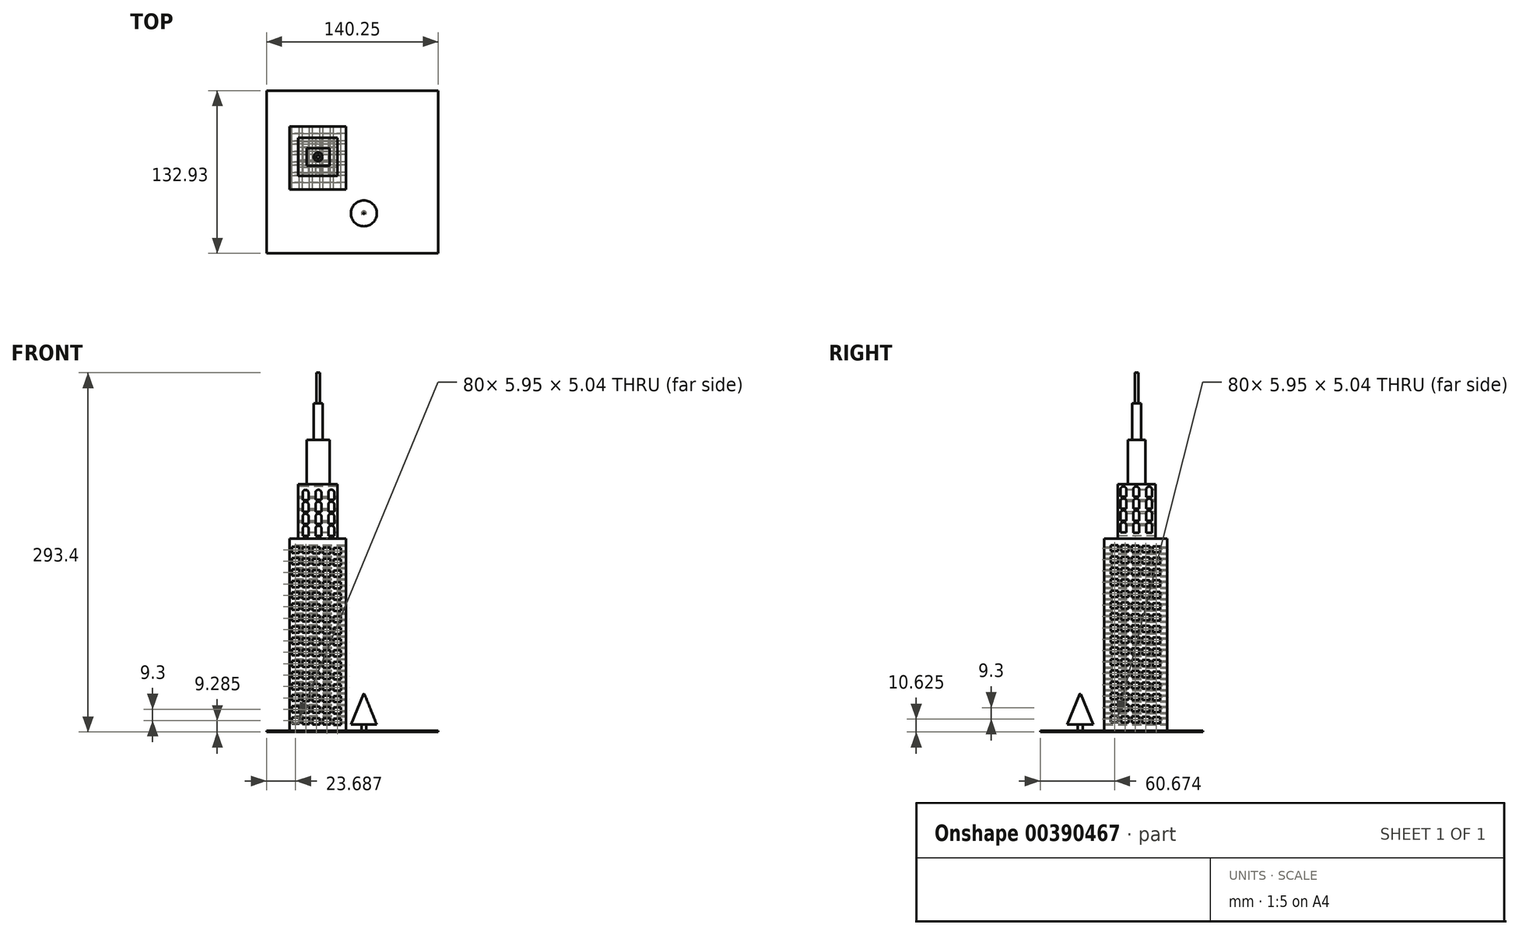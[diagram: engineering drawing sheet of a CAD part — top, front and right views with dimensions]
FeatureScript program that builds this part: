
annotation { "Feature Type Name" : "Feature", "Feature Type Description" : "" }
export const myFeature = defineFeature(function(context is Context, id is Id, definition is map)
    precondition{}
    {
        {
            var Q0;
            Q0=qCreatedBy(makeId("Top.planeOp"),FACE);
            var sketch = newSketch(context, id + "F0", { "sketchPlane" : qUnion([Q0])});
            skLineSegment(sketch, "E0.bottom", {"start": v(-71.35, 69.65) * mm, "end": v(68.9, 69.65) * mm});
            skLineSegment(sketch, "E0.top", {"start": v(-71.35, -63.28) * mm, "end": v(68.9, -63.28) * mm});
            skLineSegment(sketch, "E0.left", {"start": v(-71.35, 69.65) * mm, "end": v(-71.35, -63.28) * mm});
            skLineSegment(sketch, "E0.right", {"start": v(68.9, 69.65) * mm, "end": v(68.9, -63.28) * mm});
            skSolve(sketch);
        }
        {
            var Q0;
            Q0=makeQuery(id+"F0.imprint","IMPRINT",FACE,{"disambiguationData":[TD([[makeQuery(id+"F0.imprint","IMPRINT",EDGE,{"derivedFrom":sQuery(id+"F0.wireOp",EDGE,"E0.bottom")}),-1.0]])]});
            extrude(context, id + "F1", {"entities" : qUnion([Q0]), "depth" : 1 * mm});
        }
        {
            var Q0;
            Q0=makeQuery(id+"F1.opExtrude","CAP_FACE",FACE,{"disambiguationData":[OSD([sQuery(id+"F0.wireOp",EDGE,"E0.bottom"),sQuery(id+"F0.wireOp",EDGE,"E0.top"),sQuery(id+"F0.wireOp",EDGE,"E0.left"),sQuery(id+"F0.wireOp",EDGE,"E0.right")])],"isStart":false});
            var sketch = newSketch(context, id + "F2", { "sketchPlane" : qUnion([Q0])});
            skLineSegment(sketch, "E1.bottom", {"start": v(-52.6, 40.36) * mm, "end": v(-6.42, 40.36) * mm});
            skLineSegment(sketch, "E1.top", {"start": v(-52.6, -11.24) * mm, "end": v(-6.42, -11.24) * mm});
            skLineSegment(sketch, "E1.left", {"start": v(-52.6, 40.36) * mm, "end": v(-52.6, -11.24) * mm});
            skLineSegment(sketch, "E1.right", {"start": v(-6.42, 40.36) * mm, "end": v(-6.42, -11.24) * mm});
            skSolve(sketch);
        }
        {
            var Q0;
            Q0=makeQuery(id+"F2.imprint","IMPRINT",FACE,{"disambiguationData":[TD([[makeQuery(id+"F2.imprint","IMPRINT",EDGE,{"derivedFrom":sQuery(id+"F2.wireOp",EDGE,"E1.bottom")}),-1.0]])]});
            extrude(context, id + "F3", {"entities" : qUnion([Q0]), "operationType" : NewBodyOperationType.ADD, "depth" : 157 * mm});
        }
        {
            var Q0;
            Q0=makeQuery(id+"F3.opExtrude","CAP_FACE",FACE,{"disambiguationData":[OSD([sQuery(id+"F2.wireOp",EDGE,"E1.bottom"),sQuery(id+"F2.wireOp",EDGE,"E1.top"),sQuery(id+"F2.wireOp",EDGE,"E1.left"),sQuery(id+"F2.wireOp",EDGE,"E1.right")])],"isStart":false});
            var sketch = newSketch(context, id + "F4", { "sketchPlane" : qUnion([Q0])});
            skLineSegment(sketch, "E2.bottom", {"start": v(-45.38, 30.95) * mm, "end": v(-13.57, 30.95) * mm});
            skLineSegment(sketch, "E2.top", {"start": v(-45.38, 0) * mm, "end": v(-13.57, 0) * mm});
            skLineSegment(sketch, "E2.left", {"start": v(-45.38, 30.95) * mm, "end": v(-45.38, 0) * mm});
            skLineSegment(sketch, "E2.right", {"start": v(-13.57, 30.95) * mm, "end": v(-13.57, 0) * mm});
            skSolve(sketch);
        }
        {
            var Q0;
            Q0=makeQuery(id+"F4.imprint","IMPRINT",FACE,{"disambiguationData":[TD([[makeQuery(id+"F4.imprint","IMPRINT",EDGE,{"derivedFrom":sQuery(id+"F4.wireOp",EDGE,"E2.bottom")}),-1.0]])]});
            extrude(context, id + "F5", {"entities" : qUnion([Q0]), "operationType" : NewBodyOperationType.ADD, "depth" : 44.3 * mm});
        }
        {
            var Q0;
            Q0=makeQuery(id+"F5.opExtrude","CAP_FACE",FACE,{"disambiguationData":[OSD([sQuery(id+"F4.wireOp",EDGE,"E2.bottom"),sQuery(id+"F4.wireOp",EDGE,"E2.top"),sQuery(id+"F4.wireOp",EDGE,"E2.left"),sQuery(id+"F4.wireOp",EDGE,"E2.right")])],"isStart":false});
            var sketch = newSketch(context, id + "F6", { "sketchPlane" : qUnion([Q0])});
            skLineSegment(sketch, "E3.bottom", {"start": v(-38.58, 22.65) * mm, "end": v(-19.77, 22.65) * mm});
            skLineSegment(sketch, "E3.top", {"start": v(-38.58, 8.27) * mm, "end": v(-19.77, 8.27) * mm});
            skLineSegment(sketch, "E3.left", {"start": v(-38.58, 22.65) * mm, "end": v(-38.58, 8.27) * mm});
            skLineSegment(sketch, "E3.right", {"start": v(-19.77, 22.65) * mm, "end": v(-19.77, 8.27) * mm});
            skSolve(sketch);
        }
        {
            var Q0;
            Q0=makeQuery(id+"F6.imprint","IMPRINT",FACE,{"disambiguationData":[TD([[makeQuery(id+"F6.imprint","IMPRINT",EDGE,{"derivedFrom":sQuery(id+"F6.wireOp",EDGE,"E3.bottom")}),-1.0]])]});
            extrude(context, id + "F7", {"entities" : qUnion([Q0]), "operationType" : NewBodyOperationType.ADD, "depth" : 36.3 * mm});
        }
        {
            var Q0;
            Q0=makeQuery(id+"F7.opExtrude","CAP_FACE",FACE,{"disambiguationData":[OSD([sQuery(id+"F6.wireOp",EDGE,"E3.bottom"),sQuery(id+"F6.wireOp",EDGE,"E3.top"),sQuery(id+"F6.wireOp",EDGE,"E3.left"),sQuery(id+"F6.wireOp",EDGE,"E3.right")])],"isStart":false});
            var sketch = newSketch(context, id + "F8", { "sketchPlane" : qUnion([Q0])});
            skCircle(sketch, "E4", {"center": v(-29.18, 15.46) * mm, "radius": 3.56 * mm});
            skPoint(sketch, "E4.centerSnap0", {"position": v(-19.77, 15.46) * mm});
            skPoint(sketch, "E4.centerSnap1", {"position": v(-29.18, 22.65) * mm});
            skSolve(sketch);
        }
        {
            var Q0;
            Q0=makeQuery(id+"F8.imprint","IMPRINT",FACE,{"disambiguationData":[TD([[makeQuery(id+"F8.imprint","IMPRINT",EDGE,{"derivedFrom":sQuery(id+"F8.wireOp",EDGE,"E4")}),1.0]])]});
            extrude(context, id + "F9", {"entities" : qUnion([Q0]), "operationType" : NewBodyOperationType.ADD, "depth" : 29.8 * mm});
        }
        {
            var Q0;
            Q0=makeQuery(id+"F9.opExtrude","CAP_FACE",FACE,{"disambiguationData":[OSD([sQuery(id+"F8.wireOp",EDGE,"E4")])],"isStart":false});
            var sketch = newSketch(context, id + "F10", { "sketchPlane" : qUnion([Q0])});
            skCircle(sketch, "E5", {"center": v(-29.18, 15.46) * mm, "radius": 1.47 * mm});
            skSolve(sketch);
        }
        {
            var Q0;
            Q0=makeQuery(id+"F10.imprint","IMPRINT",FACE,{"disambiguationData":[TD([[makeQuery(id+"F10.imprint","IMPRINT",EDGE,{"derivedFrom":sQuery(id+"F10.wireOp",EDGE,"E5")}),1.0]])]});
            extrude(context, id + "F11", {"entities" : qUnion([Q0]), "operationType" : NewBodyOperationType.ADD, "depth" : 25 * mm});
        }
        {
            var Q0;
            Q0=makeQuery(id+"F3.opExtrude","SWEPT_FACE",FACE,{"disambiguationData":[OSD([sQuery(id+"F2.wireOp",EDGE,"E1.bottom")])]});
            var sketch = newSketch(context, id + "F12", { "sketchPlane" : qUnion([Q0])});
            skLineSegment(sketch, "E6.bottom", {"start": v(10.57, 10.87) * mm, "end": v(16.52, 10.87) * mm});
            skLineSegment(sketch, "E6.top", {"start": v(10.57, 5.83) * mm, "end": v(16.52, 5.83) * mm});
            skLineSegment(sketch, "E6.left", {"start": v(10.57, 10.87) * mm, "end": v(10.57, 5.83) * mm});
            skLineSegment(sketch, "E6.right", {"start": v(16.52, 10.87) * mm, "end": v(16.52, 5.83) * mm});
            skLineSegment(sketch, "E7.0.1.0", {"start": v(10.57, 20.17) * mm, "end": v(16.52, 20.17) * mm});
            skLineSegment(sketch, "E7.0.1.1", {"start": v(16.52, 20.17) * mm, "end": v(16.52, 15.13) * mm});
            skLineSegment(sketch, "E7.0.1.2", {"start": v(10.57, 15.13) * mm, "end": v(16.52, 15.13) * mm});
            skLineSegment(sketch, "E7.0.1.3", {"start": v(10.57, 20.17) * mm, "end": v(10.57, 15.13) * mm});
            skLineSegment(sketch, "E7.0.2.0", {"start": v(10.57, 29.47) * mm, "end": v(16.52, 29.47) * mm});
            skLineSegment(sketch, "E7.0.2.1", {"start": v(16.52, 29.47) * mm, "end": v(16.52, 24.43) * mm});
            skLineSegment(sketch, "E7.0.2.2", {"start": v(10.57, 24.43) * mm, "end": v(16.52, 24.43) * mm});
            skLineSegment(sketch, "E7.0.2.3", {"start": v(10.57, 29.47) * mm, "end": v(10.57, 24.43) * mm});
            skLineSegment(sketch, "E7.0.3.0", {"start": v(10.57, 38.77) * mm, "end": v(16.52, 38.77) * mm});
            skLineSegment(sketch, "E7.0.3.1", {"start": v(16.52, 38.77) * mm, "end": v(16.52, 33.73) * mm});
            skLineSegment(sketch, "E7.0.3.2", {"start": v(10.57, 33.73) * mm, "end": v(16.52, 33.73) * mm});
            skLineSegment(sketch, "E7.0.3.3", {"start": v(10.57, 38.77) * mm, "end": v(10.57, 33.73) * mm});
            skLineSegment(sketch, "E7.0.4.0", {"start": v(10.57, 48.07) * mm, "end": v(16.52, 48.07) * mm});
            skLineSegment(sketch, "E7.0.4.1", {"start": v(16.52, 48.07) * mm, "end": v(16.52, 43.03) * mm});
            skLineSegment(sketch, "E7.0.4.2", {"start": v(10.57, 43.03) * mm, "end": v(16.52, 43.03) * mm});
            skLineSegment(sketch, "E7.0.4.3", {"start": v(10.57, 48.07) * mm, "end": v(10.57, 43.03) * mm});
            skLineSegment(sketch, "E7.0.5.0", {"start": v(10.57, 57.37) * mm, "end": v(16.52, 57.37) * mm});
            skLineSegment(sketch, "E7.0.5.1", {"start": v(16.52, 57.37) * mm, "end": v(16.52, 52.33) * mm});
            skLineSegment(sketch, "E7.0.5.2", {"start": v(10.57, 52.33) * mm, "end": v(16.52, 52.33) * mm});
            skLineSegment(sketch, "E7.0.5.3", {"start": v(10.57, 57.37) * mm, "end": v(10.57, 52.33) * mm});
            skLineSegment(sketch, "E7.0.6.0", {"start": v(10.57, 66.67) * mm, "end": v(16.52, 66.67) * mm});
            skLineSegment(sketch, "E7.0.6.1", {"start": v(16.52, 66.67) * mm, "end": v(16.52, 61.63) * mm});
            skLineSegment(sketch, "E7.0.6.2", {"start": v(10.57, 61.63) * mm, "end": v(16.52, 61.63) * mm});
            skLineSegment(sketch, "E7.0.6.3", {"start": v(10.57, 66.67) * mm, "end": v(10.57, 61.63) * mm});
            skLineSegment(sketch, "E7.0.7.0", {"start": v(10.57, 75.97) * mm, "end": v(16.52, 75.97) * mm});
            skLineSegment(sketch, "E7.0.7.1", {"start": v(16.52, 75.97) * mm, "end": v(16.52, 70.93) * mm});
            skLineSegment(sketch, "E7.0.7.2", {"start": v(10.57, 70.93) * mm, "end": v(16.52, 70.93) * mm});
            skLineSegment(sketch, "E7.0.7.3", {"start": v(10.57, 75.97) * mm, "end": v(10.57, 70.93) * mm});
            skLineSegment(sketch, "E7.0.8.0", {"start": v(10.57, 85.27) * mm, "end": v(16.52, 85.27) * mm});
            skLineSegment(sketch, "E7.0.8.1", {"start": v(16.52, 85.27) * mm, "end": v(16.52, 80.23) * mm});
            skLineSegment(sketch, "E7.0.8.2", {"start": v(10.57, 80.23) * mm, "end": v(16.52, 80.23) * mm});
            skLineSegment(sketch, "E7.0.8.3", {"start": v(10.57, 85.27) * mm, "end": v(10.57, 80.23) * mm});
            skLineSegment(sketch, "E7.0.9.0", {"start": v(10.57, 94.57) * mm, "end": v(16.52, 94.57) * mm});
            skLineSegment(sketch, "E7.0.9.1", {"start": v(16.52, 94.57) * mm, "end": v(16.52, 89.53) * mm});
            skLineSegment(sketch, "E7.0.9.2", {"start": v(10.57, 89.53) * mm, "end": v(16.52, 89.53) * mm});
            skLineSegment(sketch, "E7.0.9.3", {"start": v(10.57, 94.57) * mm, "end": v(10.57, 89.53) * mm});
            skLineSegment(sketch, "E7.1.0.0", {"start": v(19.1, 11.1) * mm, "end": v(25.05, 11.1) * mm});
            skLineSegment(sketch, "E7.1.0.1", {"start": v(25.05, 11.1) * mm, "end": v(25.05, 6.06) * mm});
            skLineSegment(sketch, "E7.1.0.2", {"start": v(19.1, 6.06) * mm, "end": v(25.05, 6.06) * mm});
            skLineSegment(sketch, "E7.1.0.3", {"start": v(19.1, 11.1) * mm, "end": v(19.1, 6.06) * mm});
            skLineSegment(sketch, "E7.1.1.0", {"start": v(19.1, 20.4) * mm, "end": v(25.05, 20.4) * mm});
            skLineSegment(sketch, "E7.1.1.1", {"start": v(25.05, 20.4) * mm, "end": v(25.05, 15.36) * mm});
            skLineSegment(sketch, "E7.1.1.2", {"start": v(19.1, 15.36) * mm, "end": v(25.05, 15.36) * mm});
            skLineSegment(sketch, "E7.1.1.3", {"start": v(19.1, 20.4) * mm, "end": v(19.1, 15.36) * mm});
            skLineSegment(sketch, "E7.1.2.0", {"start": v(19.1, 29.7) * mm, "end": v(25.05, 29.7) * mm});
            skLineSegment(sketch, "E7.1.2.1", {"start": v(25.05, 29.7) * mm, "end": v(25.05, 24.66) * mm});
            skLineSegment(sketch, "E7.1.2.2", {"start": v(19.1, 24.66) * mm, "end": v(25.05, 24.66) * mm});
            skLineSegment(sketch, "E7.1.2.3", {"start": v(19.1, 29.7) * mm, "end": v(19.1, 24.66) * mm});
            skLineSegment(sketch, "E7.1.3.0", {"start": v(19.1, 39) * mm, "end": v(25.05, 39) * mm});
            skLineSegment(sketch, "E7.1.3.1", {"start": v(25.05, 39) * mm, "end": v(25.05, 33.96) * mm});
            skLineSegment(sketch, "E7.1.3.2", {"start": v(19.1, 33.96) * mm, "end": v(25.05, 33.96) * mm});
            skLineSegment(sketch, "E7.1.3.3", {"start": v(19.1, 39) * mm, "end": v(19.1, 33.96) * mm});
            skLineSegment(sketch, "E7.1.4.0", {"start": v(19.1, 48.3) * mm, "end": v(25.05, 48.3) * mm});
            skLineSegment(sketch, "E7.1.4.1", {"start": v(25.05, 48.3) * mm, "end": v(25.05, 43.26) * mm});
            skLineSegment(sketch, "E7.1.4.2", {"start": v(19.1, 43.26) * mm, "end": v(25.05, 43.26) * mm});
            skLineSegment(sketch, "E7.1.4.3", {"start": v(19.1, 48.3) * mm, "end": v(19.1, 43.26) * mm});
            skLineSegment(sketch, "E7.1.5.0", {"start": v(19.1, 57.6) * mm, "end": v(25.05, 57.6) * mm});
            skLineSegment(sketch, "E7.1.5.1", {"start": v(25.05, 57.6) * mm, "end": v(25.05, 52.56) * mm});
            skLineSegment(sketch, "E7.1.5.2", {"start": v(19.1, 52.56) * mm, "end": v(25.05, 52.56) * mm});
            skLineSegment(sketch, "E7.1.5.3", {"start": v(19.1, 57.6) * mm, "end": v(19.1, 52.56) * mm});
            skLineSegment(sketch, "E7.1.6.0", {"start": v(19.1, 66.9) * mm, "end": v(25.05, 66.9) * mm});
            skLineSegment(sketch, "E7.1.6.1", {"start": v(25.05, 66.9) * mm, "end": v(25.05, 61.86) * mm});
            skLineSegment(sketch, "E7.1.6.2", {"start": v(19.1, 61.86) * mm, "end": v(25.05, 61.86) * mm});
            skLineSegment(sketch, "E7.1.6.3", {"start": v(19.1, 66.9) * mm, "end": v(19.1, 61.86) * mm});
            skLineSegment(sketch, "E7.1.7.0", {"start": v(19.1, 76.2) * mm, "end": v(25.05, 76.2) * mm});
            skLineSegment(sketch, "E7.1.7.1", {"start": v(25.05, 76.2) * mm, "end": v(25.05, 71.16) * mm});
            skLineSegment(sketch, "E7.1.7.2", {"start": v(19.1, 71.16) * mm, "end": v(25.05, 71.16) * mm});
            skLineSegment(sketch, "E7.1.7.3", {"start": v(19.1, 76.2) * mm, "end": v(19.1, 71.16) * mm});
            skLineSegment(sketch, "E7.1.8.0", {"start": v(19.1, 85.5) * mm, "end": v(25.05, 85.5) * mm});
            skLineSegment(sketch, "E7.1.8.1", {"start": v(25.05, 85.5) * mm, "end": v(25.05, 80.46) * mm});
            skLineSegment(sketch, "E7.1.8.2", {"start": v(19.1, 80.46) * mm, "end": v(25.05, 80.46) * mm});
            skLineSegment(sketch, "E7.1.8.3", {"start": v(19.1, 85.5) * mm, "end": v(19.1, 80.46) * mm});
            skLineSegment(sketch, "E7.1.9.0", {"start": v(19.1, 94.8) * mm, "end": v(25.05, 94.8) * mm});
            skLineSegment(sketch, "E7.1.9.1", {"start": v(25.05, 94.8) * mm, "end": v(25.05, 89.76) * mm});
            skLineSegment(sketch, "E7.1.9.2", {"start": v(19.1, 89.76) * mm, "end": v(25.05, 89.76) * mm});
            skLineSegment(sketch, "E7.1.9.3", {"start": v(19.1, 94.8) * mm, "end": v(19.1, 89.76) * mm});
            skLineSegment(sketch, "E7.2.0.0", {"start": v(27.63, 11.33) * mm, "end": v(33.58, 11.33) * mm});
            skLineSegment(sketch, "E7.2.0.1", {"start": v(33.58, 11.33) * mm, "end": v(33.58, 6.3) * mm});
            skLineSegment(sketch, "E7.2.0.2", {"start": v(27.63, 6.3) * mm, "end": v(33.58, 6.3) * mm});
            skLineSegment(sketch, "E7.2.0.3", {"start": v(27.63, 11.33) * mm, "end": v(27.63, 6.3) * mm});
            skLineSegment(sketch, "E7.2.1.0", {"start": v(27.63, 20.63) * mm, "end": v(33.58, 20.63) * mm});
            skLineSegment(sketch, "E7.2.1.1", {"start": v(33.58, 20.63) * mm, "end": v(33.58, 15.6) * mm});
            skLineSegment(sketch, "E7.2.1.2", {"start": v(27.63, 15.6) * mm, "end": v(33.58, 15.6) * mm});
            skLineSegment(sketch, "E7.2.1.3", {"start": v(27.63, 20.63) * mm, "end": v(27.63, 15.6) * mm});
            skLineSegment(sketch, "E7.2.2.0", {"start": v(27.63, 29.93) * mm, "end": v(33.58, 29.93) * mm});
            skLineSegment(sketch, "E7.2.2.1", {"start": v(33.58, 29.93) * mm, "end": v(33.58, 24.9) * mm});
            skLineSegment(sketch, "E7.2.2.2", {"start": v(27.63, 24.9) * mm, "end": v(33.58, 24.9) * mm});
            skLineSegment(sketch, "E7.2.2.3", {"start": v(27.63, 29.93) * mm, "end": v(27.63, 24.9) * mm});
            skLineSegment(sketch, "E7.2.3.0", {"start": v(27.63, 39.23) * mm, "end": v(33.58, 39.23) * mm});
            skLineSegment(sketch, "E7.2.3.1", {"start": v(33.58, 39.23) * mm, "end": v(33.58, 34.2) * mm});
            skLineSegment(sketch, "E7.2.3.2", {"start": v(27.63, 34.2) * mm, "end": v(33.58, 34.2) * mm});
            skLineSegment(sketch, "E7.2.3.3", {"start": v(27.63, 39.23) * mm, "end": v(27.63, 34.2) * mm});
            skLineSegment(sketch, "E7.2.4.0", {"start": v(27.63, 48.53) * mm, "end": v(33.58, 48.53) * mm});
            skLineSegment(sketch, "E7.2.4.1", {"start": v(33.58, 48.53) * mm, "end": v(33.58, 43.5) * mm});
            skLineSegment(sketch, "E7.2.4.2", {"start": v(27.63, 43.5) * mm, "end": v(33.58, 43.5) * mm});
            skLineSegment(sketch, "E7.2.4.3", {"start": v(27.63, 48.53) * mm, "end": v(27.63, 43.5) * mm});
            skLineSegment(sketch, "E7.2.5.0", {"start": v(27.63, 57.83) * mm, "end": v(33.58, 57.83) * mm});
            skLineSegment(sketch, "E7.2.5.1", {"start": v(33.58, 57.83) * mm, "end": v(33.58, 52.8) * mm});
            skLineSegment(sketch, "E7.2.5.2", {"start": v(27.63, 52.8) * mm, "end": v(33.58, 52.8) * mm});
            skLineSegment(sketch, "E7.2.5.3", {"start": v(27.63, 57.83) * mm, "end": v(27.63, 52.8) * mm});
            skLineSegment(sketch, "E7.2.6.0", {"start": v(27.63, 67.13) * mm, "end": v(33.58, 67.13) * mm});
            skLineSegment(sketch, "E7.2.6.1", {"start": v(33.58, 67.13) * mm, "end": v(33.58, 62.1) * mm});
            skLineSegment(sketch, "E7.2.6.2", {"start": v(27.63, 62.1) * mm, "end": v(33.58, 62.1) * mm});
            skLineSegment(sketch, "E7.2.6.3", {"start": v(27.63, 67.13) * mm, "end": v(27.63, 62.1) * mm});
            skLineSegment(sketch, "E7.2.7.0", {"start": v(27.63, 76.43) * mm, "end": v(33.58, 76.43) * mm});
            skLineSegment(sketch, "E7.2.7.1", {"start": v(33.58, 76.43) * mm, "end": v(33.58, 71.4) * mm});
            skLineSegment(sketch, "E7.2.7.2", {"start": v(27.63, 71.4) * mm, "end": v(33.58, 71.4) * mm});
            skLineSegment(sketch, "E7.2.7.3", {"start": v(27.63, 76.43) * mm, "end": v(27.63, 71.4) * mm});
            skLineSegment(sketch, "E7.2.8.0", {"start": v(27.63, 85.73) * mm, "end": v(33.58, 85.73) * mm});
            skLineSegment(sketch, "E7.2.8.1", {"start": v(33.58, 85.73) * mm, "end": v(33.58, 80.7) * mm});
            skLineSegment(sketch, "E7.2.8.2", {"start": v(27.63, 80.7) * mm, "end": v(33.58, 80.7) * mm});
            skLineSegment(sketch, "E7.2.8.3", {"start": v(27.63, 85.73) * mm, "end": v(27.63, 80.7) * mm});
            skLineSegment(sketch, "E7.2.9.0", {"start": v(27.63, 95.03) * mm, "end": v(33.58, 95.03) * mm});
            skLineSegment(sketch, "E7.2.9.1", {"start": v(33.58, 95.03) * mm, "end": v(33.58, 90) * mm});
            skLineSegment(sketch, "E7.2.9.2", {"start": v(27.63, 90) * mm, "end": v(33.58, 90) * mm});
            skLineSegment(sketch, "E7.2.9.3", {"start": v(27.63, 95.03) * mm, "end": v(27.63, 90) * mm});
            skLineSegment(sketch, "E7.3.0.0", {"start": v(36.16, 11.57) * mm, "end": v(42.11, 11.57) * mm});
            skLineSegment(sketch, "E7.3.0.1", {"start": v(42.11, 11.57) * mm, "end": v(42.11, 6.53) * mm});
            skLineSegment(sketch, "E7.3.0.2", {"start": v(36.16, 6.53) * mm, "end": v(42.11, 6.53) * mm});
            skLineSegment(sketch, "E7.3.0.3", {"start": v(36.16, 11.57) * mm, "end": v(36.16, 6.53) * mm});
            skLineSegment(sketch, "E7.3.1.0", {"start": v(36.16, 20.87) * mm, "end": v(42.11, 20.87) * mm});
            skLineSegment(sketch, "E7.3.1.1", {"start": v(42.11, 20.87) * mm, "end": v(42.11, 15.83) * mm});
            skLineSegment(sketch, "E7.3.1.2", {"start": v(36.16, 15.83) * mm, "end": v(42.11, 15.83) * mm});
            skLineSegment(sketch, "E7.3.1.3", {"start": v(36.16, 20.87) * mm, "end": v(36.16, 15.83) * mm});
            skLineSegment(sketch, "E7.3.2.0", {"start": v(36.16, 30.17) * mm, "end": v(42.11, 30.17) * mm});
            skLineSegment(sketch, "E7.3.2.1", {"start": v(42.11, 30.17) * mm, "end": v(42.11, 25.13) * mm});
            skLineSegment(sketch, "E7.3.2.2", {"start": v(36.16, 25.13) * mm, "end": v(42.11, 25.13) * mm});
            skLineSegment(sketch, "E7.3.2.3", {"start": v(36.16, 30.17) * mm, "end": v(36.16, 25.13) * mm});
            skLineSegment(sketch, "E7.3.3.0", {"start": v(36.16, 39.47) * mm, "end": v(42.11, 39.47) * mm});
            skLineSegment(sketch, "E7.3.3.1", {"start": v(42.11, 39.47) * mm, "end": v(42.11, 34.43) * mm});
            skLineSegment(sketch, "E7.3.3.2", {"start": v(36.16, 34.43) * mm, "end": v(42.11, 34.43) * mm});
            skLineSegment(sketch, "E7.3.3.3", {"start": v(36.16, 39.47) * mm, "end": v(36.16, 34.43) * mm});
            skLineSegment(sketch, "E7.3.4.0", {"start": v(36.16, 48.77) * mm, "end": v(42.11, 48.77) * mm});
            skLineSegment(sketch, "E7.3.4.1", {"start": v(42.11, 48.77) * mm, "end": v(42.11, 43.73) * mm});
            skLineSegment(sketch, "E7.3.4.2", {"start": v(36.16, 43.73) * mm, "end": v(42.11, 43.73) * mm});
            skLineSegment(sketch, "E7.3.4.3", {"start": v(36.16, 48.77) * mm, "end": v(36.16, 43.73) * mm});
            skLineSegment(sketch, "E7.3.5.0", {"start": v(36.16, 58.07) * mm, "end": v(42.11, 58.07) * mm});
            skLineSegment(sketch, "E7.3.5.1", {"start": v(42.11, 58.07) * mm, "end": v(42.11, 53.03) * mm});
            skLineSegment(sketch, "E7.3.5.2", {"start": v(36.16, 53.03) * mm, "end": v(42.11, 53.03) * mm});
            skLineSegment(sketch, "E7.3.5.3", {"start": v(36.16, 58.07) * mm, "end": v(36.16, 53.03) * mm});
            skLineSegment(sketch, "E7.3.6.0", {"start": v(36.16, 67.37) * mm, "end": v(42.11, 67.37) * mm});
            skLineSegment(sketch, "E7.3.6.1", {"start": v(42.11, 67.37) * mm, "end": v(42.11, 62.33) * mm});
            skLineSegment(sketch, "E7.3.6.2", {"start": v(36.16, 62.33) * mm, "end": v(42.11, 62.33) * mm});
            skLineSegment(sketch, "E7.3.6.3", {"start": v(36.16, 67.37) * mm, "end": v(36.16, 62.33) * mm});
            skLineSegment(sketch, "E7.3.7.0", {"start": v(36.16, 76.67) * mm, "end": v(42.11, 76.67) * mm});
            skLineSegment(sketch, "E7.3.7.1", {"start": v(42.11, 76.67) * mm, "end": v(42.11, 71.63) * mm});
            skLineSegment(sketch, "E7.3.7.2", {"start": v(36.16, 71.63) * mm, "end": v(42.11, 71.63) * mm});
            skLineSegment(sketch, "E7.3.7.3", {"start": v(36.16, 76.67) * mm, "end": v(36.16, 71.63) * mm});
            skLineSegment(sketch, "E7.3.8.0", {"start": v(36.16, 85.97) * mm, "end": v(42.11, 85.97) * mm});
            skLineSegment(sketch, "E7.3.8.1", {"start": v(42.11, 85.97) * mm, "end": v(42.11, 80.93) * mm});
            skLineSegment(sketch, "E7.3.8.2", {"start": v(36.16, 80.93) * mm, "end": v(42.11, 80.93) * mm});
            skLineSegment(sketch, "E7.3.8.3", {"start": v(36.16, 85.97) * mm, "end": v(36.16, 80.93) * mm});
            skLineSegment(sketch, "E7.3.9.0", {"start": v(36.16, 95.27) * mm, "end": v(42.11, 95.27) * mm});
            skLineSegment(sketch, "E7.3.9.1", {"start": v(42.11, 95.27) * mm, "end": v(42.11, 90.23) * mm});
            skLineSegment(sketch, "E7.3.9.2", {"start": v(36.16, 90.23) * mm, "end": v(42.11, 90.23) * mm});
            skLineSegment(sketch, "E7.3.9.3", {"start": v(36.16, 95.27) * mm, "end": v(36.16, 90.23) * mm});
            skLineSegment(sketch, "E7.4.0.0", {"start": v(44.69, 11.8) * mm, "end": v(50.64, 11.8) * mm});
            skLineSegment(sketch, "E7.4.0.1", {"start": v(50.64, 11.8) * mm, "end": v(50.64, 6.77) * mm});
            skLineSegment(sketch, "E7.4.0.2", {"start": v(44.69, 6.77) * mm, "end": v(50.64, 6.77) * mm});
            skLineSegment(sketch, "E7.4.0.3", {"start": v(44.69, 11.8) * mm, "end": v(44.69, 6.77) * mm});
            skLineSegment(sketch, "E7.4.1.0", {"start": v(44.69, 21.1) * mm, "end": v(50.64, 21.1) * mm});
            skLineSegment(sketch, "E7.4.1.1", {"start": v(50.64, 21.1) * mm, "end": v(50.64, 16.07) * mm});
            skLineSegment(sketch, "E7.4.1.2", {"start": v(44.69, 16.07) * mm, "end": v(50.64, 16.07) * mm});
            skLineSegment(sketch, "E7.4.1.3", {"start": v(44.69, 21.1) * mm, "end": v(44.69, 16.07) * mm});
            skLineSegment(sketch, "E7.4.2.0", {"start": v(44.69, 30.4) * mm, "end": v(50.64, 30.4) * mm});
            skLineSegment(sketch, "E7.4.2.1", {"start": v(50.64, 30.4) * mm, "end": v(50.64, 25.37) * mm});
            skLineSegment(sketch, "E7.4.2.2", {"start": v(44.69, 25.37) * mm, "end": v(50.64, 25.37) * mm});
            skLineSegment(sketch, "E7.4.2.3", {"start": v(44.69, 30.4) * mm, "end": v(44.69, 25.37) * mm});
            skLineSegment(sketch, "E7.4.3.0", {"start": v(44.69, 39.7) * mm, "end": v(50.64, 39.7) * mm});
            skLineSegment(sketch, "E7.4.3.1", {"start": v(50.64, 39.7) * mm, "end": v(50.64, 34.67) * mm});
            skLineSegment(sketch, "E7.4.3.2", {"start": v(44.69, 34.67) * mm, "end": v(50.64, 34.67) * mm});
            skLineSegment(sketch, "E7.4.3.3", {"start": v(44.69, 39.7) * mm, "end": v(44.69, 34.67) * mm});
            skLineSegment(sketch, "E7.4.4.0", {"start": v(44.69, 49) * mm, "end": v(50.64, 49) * mm});
            skLineSegment(sketch, "E7.4.4.1", {"start": v(50.64, 49) * mm, "end": v(50.64, 43.97) * mm});
            skLineSegment(sketch, "E7.4.4.2", {"start": v(44.69, 43.97) * mm, "end": v(50.64, 43.97) * mm});
            skLineSegment(sketch, "E7.4.4.3", {"start": v(44.69, 49) * mm, "end": v(44.69, 43.97) * mm});
            skLineSegment(sketch, "E7.4.5.0", {"start": v(44.69, 58.3) * mm, "end": v(50.64, 58.3) * mm});
            skLineSegment(sketch, "E7.4.5.1", {"start": v(50.64, 58.3) * mm, "end": v(50.64, 53.27) * mm});
            skLineSegment(sketch, "E7.4.5.2", {"start": v(44.69, 53.27) * mm, "end": v(50.64, 53.27) * mm});
            skLineSegment(sketch, "E7.4.5.3", {"start": v(44.69, 58.3) * mm, "end": v(44.69, 53.27) * mm});
            skLineSegment(sketch, "E7.4.6.0", {"start": v(44.69, 67.6) * mm, "end": v(50.64, 67.6) * mm});
            skLineSegment(sketch, "E7.4.6.1", {"start": v(50.64, 67.6) * mm, "end": v(50.64, 62.57) * mm});
            skLineSegment(sketch, "E7.4.6.2", {"start": v(44.69, 62.57) * mm, "end": v(50.64, 62.57) * mm});
            skLineSegment(sketch, "E7.4.6.3", {"start": v(44.69, 67.6) * mm, "end": v(44.69, 62.57) * mm});
            skLineSegment(sketch, "E7.4.7.0", {"start": v(44.69, 76.9) * mm, "end": v(50.64, 76.9) * mm});
            skLineSegment(sketch, "E7.4.7.1", {"start": v(50.64, 76.9) * mm, "end": v(50.64, 71.87) * mm});
            skLineSegment(sketch, "E7.4.7.2", {"start": v(44.69, 71.87) * mm, "end": v(50.64, 71.87) * mm});
            skLineSegment(sketch, "E7.4.7.3", {"start": v(44.69, 76.9) * mm, "end": v(44.69, 71.87) * mm});
            skLineSegment(sketch, "E7.4.8.0", {"start": v(44.69, 86.2) * mm, "end": v(50.64, 86.2) * mm});
            skLineSegment(sketch, "E7.4.8.1", {"start": v(50.64, 86.2) * mm, "end": v(50.64, 81.17) * mm});
            skLineSegment(sketch, "E7.4.8.2", {"start": v(44.69, 81.17) * mm, "end": v(50.64, 81.17) * mm});
            skLineSegment(sketch, "E7.4.8.3", {"start": v(44.69, 86.2) * mm, "end": v(44.69, 81.17) * mm});
            skLineSegment(sketch, "E7.4.9.0", {"start": v(44.69, 95.5) * mm, "end": v(50.64, 95.5) * mm});
            skLineSegment(sketch, "E7.4.9.1", {"start": v(50.64, 95.5) * mm, "end": v(50.64, 90.47) * mm});
            skLineSegment(sketch, "E7.4.9.2", {"start": v(44.69, 90.47) * mm, "end": v(50.64, 90.47) * mm});
            skLineSegment(sketch, "E7.4.9.3", {"start": v(44.69, 95.5) * mm, "end": v(44.69, 90.47) * mm});
            skLineSegment(sketch, "E7.direction1", {"start": v(10.57, 10.87) * mm, "end": v(19.1, 11.1) * mm, "construction": true});
            skLineSegment(sketch, "E7.direction2", {"start": v(10.57, 10.87) * mm, "end": v(10.57, 20.17) * mm, "construction": true});
            skLineSegment(sketch, "E8.0.0.10", {"start": v(10.57, 103.87) * mm, "end": v(16.52, 103.87) * mm});
            skLineSegment(sketch, "E8.3.0.10", {"start": v(16.52, 103.87) * mm, "end": v(16.52, 98.83) * mm});
            skLineSegment(sketch, "E8.6.0.10", {"start": v(10.57, 98.83) * mm, "end": v(16.52, 98.83) * mm});
            skLineSegment(sketch, "E8.9.0.10", {"start": v(10.57, 103.87) * mm, "end": v(10.57, 98.83) * mm});
            skLineSegment(sketch, "E8.0.0.11", {"start": v(10.57, 113.17) * mm, "end": v(16.52, 113.17) * mm});
            skLineSegment(sketch, "E8.3.0.11", {"start": v(16.52, 113.17) * mm, "end": v(16.52, 108.13) * mm});
            skLineSegment(sketch, "E8.6.0.11", {"start": v(10.57, 108.13) * mm, "end": v(16.52, 108.13) * mm});
            skLineSegment(sketch, "E8.9.0.11", {"start": v(10.57, 113.17) * mm, "end": v(10.57, 108.13) * mm});
            skLineSegment(sketch, "E8.0.0.12", {"start": v(10.57, 122.47) * mm, "end": v(16.52, 122.47) * mm});
            skLineSegment(sketch, "E8.3.0.12", {"start": v(16.52, 122.47) * mm, "end": v(16.52, 117.43) * mm});
            skLineSegment(sketch, "E8.6.0.12", {"start": v(10.57, 117.43) * mm, "end": v(16.52, 117.43) * mm});
            skLineSegment(sketch, "E8.9.0.12", {"start": v(10.57, 122.47) * mm, "end": v(10.57, 117.43) * mm});
            skLineSegment(sketch, "E8.0.0.13", {"start": v(10.57, 131.77) * mm, "end": v(16.52, 131.77) * mm});
            skLineSegment(sketch, "E8.3.0.13", {"start": v(16.52, 131.77) * mm, "end": v(16.52, 126.73) * mm});
            skLineSegment(sketch, "E8.6.0.13", {"start": v(10.57, 126.73) * mm, "end": v(16.52, 126.73) * mm});
            skLineSegment(sketch, "E8.9.0.13", {"start": v(10.57, 131.77) * mm, "end": v(10.57, 126.73) * mm});
            skLineSegment(sketch, "E8.0.0.14", {"start": v(10.57, 141.07) * mm, "end": v(16.52, 141.07) * mm});
            skLineSegment(sketch, "E8.3.0.14", {"start": v(16.52, 141.07) * mm, "end": v(16.52, 136.03) * mm});
            skLineSegment(sketch, "E8.6.0.14", {"start": v(10.57, 136.03) * mm, "end": v(16.52, 136.03) * mm});
            skLineSegment(sketch, "E8.9.0.14", {"start": v(10.57, 141.07) * mm, "end": v(10.57, 136.03) * mm});
            skLineSegment(sketch, "E8.0.1.10", {"start": v(19.1, 104.1) * mm, "end": v(25.05, 104.1) * mm});
            skLineSegment(sketch, "E8.3.1.10", {"start": v(25.05, 104.1) * mm, "end": v(25.05, 99.06) * mm});
            skLineSegment(sketch, "E8.6.1.10", {"start": v(19.1, 99.06) * mm, "end": v(25.05, 99.06) * mm});
            skLineSegment(sketch, "E8.9.1.10", {"start": v(19.1, 104.1) * mm, "end": v(19.1, 99.06) * mm});
            skLineSegment(sketch, "E8.0.1.11", {"start": v(19.1, 113.4) * mm, "end": v(25.05, 113.4) * mm});
            skLineSegment(sketch, "E8.3.1.11", {"start": v(25.05, 113.4) * mm, "end": v(25.05, 108.36) * mm});
            skLineSegment(sketch, "E8.6.1.11", {"start": v(19.1, 108.36) * mm, "end": v(25.05, 108.36) * mm});
            skLineSegment(sketch, "E8.9.1.11", {"start": v(19.1, 113.4) * mm, "end": v(19.1, 108.36) * mm});
            skLineSegment(sketch, "E8.0.1.12", {"start": v(19.1, 122.7) * mm, "end": v(25.05, 122.7) * mm});
            skLineSegment(sketch, "E8.3.1.12", {"start": v(25.05, 122.7) * mm, "end": v(25.05, 117.66) * mm});
            skLineSegment(sketch, "E8.6.1.12", {"start": v(19.1, 117.66) * mm, "end": v(25.05, 117.66) * mm});
            skLineSegment(sketch, "E8.9.1.12", {"start": v(19.1, 122.7) * mm, "end": v(19.1, 117.66) * mm});
            skLineSegment(sketch, "E8.0.1.13", {"start": v(19.1, 132) * mm, "end": v(25.05, 132) * mm});
            skLineSegment(sketch, "E8.3.1.13", {"start": v(25.05, 132) * mm, "end": v(25.05, 126.96) * mm});
            skLineSegment(sketch, "E8.6.1.13", {"start": v(19.1, 126.96) * mm, "end": v(25.05, 126.96) * mm});
            skLineSegment(sketch, "E8.9.1.13", {"start": v(19.1, 132) * mm, "end": v(19.1, 126.96) * mm});
            skLineSegment(sketch, "E8.0.1.14", {"start": v(19.1, 141.3) * mm, "end": v(25.05, 141.3) * mm});
            skLineSegment(sketch, "E8.3.1.14", {"start": v(25.05, 141.3) * mm, "end": v(25.05, 136.26) * mm});
            skLineSegment(sketch, "E8.6.1.14", {"start": v(19.1, 136.26) * mm, "end": v(25.05, 136.26) * mm});
            skLineSegment(sketch, "E8.9.1.14", {"start": v(19.1, 141.3) * mm, "end": v(19.1, 136.26) * mm});
            skLineSegment(sketch, "E8.0.2.10", {"start": v(27.63, 104.33) * mm, "end": v(33.58, 104.33) * mm});
            skLineSegment(sketch, "E8.3.2.10", {"start": v(33.58, 104.33) * mm, "end": v(33.58, 99.3) * mm});
            skLineSegment(sketch, "E8.6.2.10", {"start": v(27.63, 99.3) * mm, "end": v(33.58, 99.3) * mm});
            skLineSegment(sketch, "E8.9.2.10", {"start": v(27.63, 104.33) * mm, "end": v(27.63, 99.3) * mm});
            skLineSegment(sketch, "E8.0.2.11", {"start": v(27.63, 113.63) * mm, "end": v(33.58, 113.63) * mm});
            skLineSegment(sketch, "E8.3.2.11", {"start": v(33.58, 113.63) * mm, "end": v(33.58, 108.6) * mm});
            skLineSegment(sketch, "E8.6.2.11", {"start": v(27.63, 108.6) * mm, "end": v(33.58, 108.6) * mm});
            skLineSegment(sketch, "E8.9.2.11", {"start": v(27.63, 113.63) * mm, "end": v(27.63, 108.6) * mm});
            skLineSegment(sketch, "E8.0.2.12", {"start": v(27.63, 122.93) * mm, "end": v(33.58, 122.93) * mm});
            skLineSegment(sketch, "E8.3.2.12", {"start": v(33.58, 122.93) * mm, "end": v(33.58, 117.9) * mm});
            skLineSegment(sketch, "E8.6.2.12", {"start": v(27.63, 117.9) * mm, "end": v(33.58, 117.9) * mm});
            skLineSegment(sketch, "E8.9.2.12", {"start": v(27.63, 122.93) * mm, "end": v(27.63, 117.9) * mm});
            skLineSegment(sketch, "E8.0.2.13", {"start": v(27.63, 132.23) * mm, "end": v(33.58, 132.23) * mm});
            skLineSegment(sketch, "E8.3.2.13", {"start": v(33.58, 132.23) * mm, "end": v(33.58, 127.2) * mm});
            skLineSegment(sketch, "E8.6.2.13", {"start": v(27.63, 127.2) * mm, "end": v(33.58, 127.2) * mm});
            skLineSegment(sketch, "E8.9.2.13", {"start": v(27.63, 132.23) * mm, "end": v(27.63, 127.2) * mm});
            skLineSegment(sketch, "E8.0.2.14", {"start": v(27.63, 141.53) * mm, "end": v(33.58, 141.53) * mm});
            skLineSegment(sketch, "E8.3.2.14", {"start": v(33.58, 141.53) * mm, "end": v(33.58, 136.5) * mm});
            skLineSegment(sketch, "E8.6.2.14", {"start": v(27.63, 136.5) * mm, "end": v(33.58, 136.5) * mm});
            skLineSegment(sketch, "E8.9.2.14", {"start": v(27.63, 141.53) * mm, "end": v(27.63, 136.5) * mm});
            skLineSegment(sketch, "E8.0.3.10", {"start": v(36.16, 104.57) * mm, "end": v(42.11, 104.57) * mm});
            skLineSegment(sketch, "E8.3.3.10", {"start": v(42.11, 104.57) * mm, "end": v(42.11, 99.53) * mm});
            skLineSegment(sketch, "E8.6.3.10", {"start": v(36.16, 99.53) * mm, "end": v(42.11, 99.53) * mm});
            skLineSegment(sketch, "E8.9.3.10", {"start": v(36.16, 104.57) * mm, "end": v(36.16, 99.53) * mm});
            skLineSegment(sketch, "E8.0.3.11", {"start": v(36.16, 113.87) * mm, "end": v(42.11, 113.87) * mm});
            skLineSegment(sketch, "E8.3.3.11", {"start": v(42.11, 113.87) * mm, "end": v(42.11, 108.83) * mm});
            skLineSegment(sketch, "E8.6.3.11", {"start": v(36.16, 108.83) * mm, "end": v(42.11, 108.83) * mm});
            skLineSegment(sketch, "E8.9.3.11", {"start": v(36.16, 113.87) * mm, "end": v(36.16, 108.83) * mm});
            skLineSegment(sketch, "E8.0.3.12", {"start": v(36.16, 123.17) * mm, "end": v(42.11, 123.17) * mm});
            skLineSegment(sketch, "E8.3.3.12", {"start": v(42.11, 123.17) * mm, "end": v(42.11, 118.13) * mm});
            skLineSegment(sketch, "E8.6.3.12", {"start": v(36.16, 118.13) * mm, "end": v(42.11, 118.13) * mm});
            skLineSegment(sketch, "E8.9.3.12", {"start": v(36.16, 123.17) * mm, "end": v(36.16, 118.13) * mm});
            skLineSegment(sketch, "E8.0.3.13", {"start": v(36.16, 132.47) * mm, "end": v(42.11, 132.47) * mm});
            skLineSegment(sketch, "E8.3.3.13", {"start": v(42.11, 132.47) * mm, "end": v(42.11, 127.43) * mm});
            skLineSegment(sketch, "E8.6.3.13", {"start": v(36.16, 127.43) * mm, "end": v(42.11, 127.43) * mm});
            skLineSegment(sketch, "E8.9.3.13", {"start": v(36.16, 132.47) * mm, "end": v(36.16, 127.43) * mm});
            skLineSegment(sketch, "E8.0.3.14", {"start": v(36.16, 141.77) * mm, "end": v(42.11, 141.77) * mm});
            skLineSegment(sketch, "E8.3.3.14", {"start": v(42.11, 141.77) * mm, "end": v(42.11, 136.73) * mm});
            skLineSegment(sketch, "E8.6.3.14", {"start": v(36.16, 136.73) * mm, "end": v(42.11, 136.73) * mm});
            skLineSegment(sketch, "E8.9.3.14", {"start": v(36.16, 141.77) * mm, "end": v(36.16, 136.73) * mm});
            skLineSegment(sketch, "E8.0.4.10", {"start": v(44.69, 104.8) * mm, "end": v(50.64, 104.8) * mm});
            skLineSegment(sketch, "E8.3.4.10", {"start": v(50.64, 104.8) * mm, "end": v(50.64, 99.77) * mm});
            skLineSegment(sketch, "E8.6.4.10", {"start": v(44.69, 99.77) * mm, "end": v(50.64, 99.77) * mm});
            skLineSegment(sketch, "E8.9.4.10", {"start": v(44.69, 104.8) * mm, "end": v(44.69, 99.77) * mm});
            skLineSegment(sketch, "E8.0.4.11", {"start": v(44.69, 114.1) * mm, "end": v(50.64, 114.1) * mm});
            skLineSegment(sketch, "E8.3.4.11", {"start": v(50.64, 114.1) * mm, "end": v(50.64, 109.07) * mm});
            skLineSegment(sketch, "E8.6.4.11", {"start": v(44.69, 109.07) * mm, "end": v(50.64, 109.07) * mm});
            skLineSegment(sketch, "E8.9.4.11", {"start": v(44.69, 114.1) * mm, "end": v(44.69, 109.07) * mm});
            skLineSegment(sketch, "E8.0.4.12", {"start": v(44.69, 123.4) * mm, "end": v(50.64, 123.4) * mm});
            skLineSegment(sketch, "E8.3.4.12", {"start": v(50.64, 123.4) * mm, "end": v(50.64, 118.37) * mm});
            skLineSegment(sketch, "E8.6.4.12", {"start": v(44.69, 118.37) * mm, "end": v(50.64, 118.37) * mm});
            skLineSegment(sketch, "E8.9.4.12", {"start": v(44.69, 123.4) * mm, "end": v(44.69, 118.37) * mm});
            skLineSegment(sketch, "E8.0.4.13", {"start": v(44.69, 132.7) * mm, "end": v(50.64, 132.7) * mm});
            skLineSegment(sketch, "E8.3.4.13", {"start": v(50.64, 132.7) * mm, "end": v(50.64, 127.67) * mm});
            skLineSegment(sketch, "E8.6.4.13", {"start": v(44.69, 127.67) * mm, "end": v(50.64, 127.67) * mm});
            skLineSegment(sketch, "E8.9.4.13", {"start": v(44.69, 132.7) * mm, "end": v(44.69, 127.67) * mm});
            skLineSegment(sketch, "E8.0.4.14", {"start": v(44.69, 142) * mm, "end": v(50.64, 142) * mm});
            skLineSegment(sketch, "E8.3.4.14", {"start": v(50.64, 142) * mm, "end": v(50.64, 136.97) * mm});
            skLineSegment(sketch, "E8.6.4.14", {"start": v(44.69, 136.97) * mm, "end": v(50.64, 136.97) * mm});
            skLineSegment(sketch, "E8.9.4.14", {"start": v(44.69, 142) * mm, "end": v(44.69, 136.97) * mm});
            skLineSegment(sketch, "E9.0.0.15", {"start": v(10.57, 150.37) * mm, "end": v(16.52, 150.37) * mm});
            skLineSegment(sketch, "E9.3.0.15", {"start": v(16.52, 150.37) * mm, "end": v(16.52, 145.33) * mm});
            skLineSegment(sketch, "E9.6.0.15", {"start": v(10.57, 145.33) * mm, "end": v(16.52, 145.33) * mm});
            skLineSegment(sketch, "E9.9.0.15", {"start": v(10.57, 150.37) * mm, "end": v(10.57, 145.33) * mm});
            skLineSegment(sketch, "E9.0.1.15", {"start": v(19.1, 150.6) * mm, "end": v(25.05, 150.6) * mm});
            skLineSegment(sketch, "E9.3.1.15", {"start": v(25.05, 150.6) * mm, "end": v(25.05, 145.56) * mm});
            skLineSegment(sketch, "E9.6.1.15", {"start": v(19.1, 145.56) * mm, "end": v(25.05, 145.56) * mm});
            skLineSegment(sketch, "E9.9.1.15", {"start": v(19.1, 150.6) * mm, "end": v(19.1, 145.56) * mm});
            skLineSegment(sketch, "E9.0.2.15", {"start": v(27.63, 150.83) * mm, "end": v(33.58, 150.83) * mm});
            skLineSegment(sketch, "E9.3.2.15", {"start": v(33.58, 150.83) * mm, "end": v(33.58, 145.8) * mm});
            skLineSegment(sketch, "E9.6.2.15", {"start": v(27.63, 145.8) * mm, "end": v(33.58, 145.8) * mm});
            skLineSegment(sketch, "E9.9.2.15", {"start": v(27.63, 150.83) * mm, "end": v(27.63, 145.8) * mm});
            skLineSegment(sketch, "E9.0.3.15", {"start": v(36.16, 151.07) * mm, "end": v(42.11, 151.07) * mm});
            skLineSegment(sketch, "E9.3.3.15", {"start": v(42.11, 151.07) * mm, "end": v(42.11, 146.03) * mm});
            skLineSegment(sketch, "E9.6.3.15", {"start": v(36.16, 146.03) * mm, "end": v(42.11, 146.03) * mm});
            skLineSegment(sketch, "E9.9.3.15", {"start": v(36.16, 151.07) * mm, "end": v(36.16, 146.03) * mm});
            skLineSegment(sketch, "E9.0.4.15", {"start": v(44.69, 151.3) * mm, "end": v(50.64, 151.3) * mm});
            skLineSegment(sketch, "E9.3.4.15", {"start": v(50.64, 151.3) * mm, "end": v(50.64, 146.27) * mm});
            skLineSegment(sketch, "E9.6.4.15", {"start": v(44.69, 146.27) * mm, "end": v(50.64, 146.27) * mm});
            skLineSegment(sketch, "E9.9.4.15", {"start": v(44.69, 151.3) * mm, "end": v(44.69, 146.27) * mm});
            skSolve(sketch);
        }
        {
            var Q0;
            Q0 = qSketchRegion(id + "F12", true);
            extrude(context, id + "F13", {"entities" : qUnion([Q0]), "operationType" : NewBodyOperationType.REMOVE, "endBound" : BoundingType.THROUGH_ALL, "oppositeDirection" : true, "depth" : 25 * mm});
        }
        {
            var Q0;
            Q0=makeQuery(id+"F3.opExtrude","SWEPT_FACE",FACE,{"disambiguationData":[OSD([sQuery(id+"F2.wireOp",EDGE,"E1.left")])]});
            var sketch = newSketch(context, id + "F14", { "sketchPlane" : qUnion([Q0])});
            skLineSegment(sketch, "E10.bottom", {"start": v(-34.49, 12.2) * mm, "end": v(-28.53, 12.2) * mm});
            skLineSegment(sketch, "E10.top", {"start": v(-34.49, 7.17) * mm, "end": v(-28.53, 7.17) * mm});
            skLineSegment(sketch, "E10.left", {"start": v(-34.49, 12.2) * mm, "end": v(-34.49, 7.17) * mm});
            skLineSegment(sketch, "E10.right", {"start": v(-28.53, 12.2) * mm, "end": v(-28.53, 7.17) * mm});
            skLineSegment(sketch, "E11.0.1.0", {"start": v(-34.49, 21.5) * mm, "end": v(-28.53, 21.5) * mm});
            skLineSegment(sketch, "E11.0.1.1", {"start": v(-28.53, 21.5) * mm, "end": v(-28.53, 16.47) * mm});
            skLineSegment(sketch, "E11.0.1.2", {"start": v(-34.49, 16.47) * mm, "end": v(-28.53, 16.47) * mm});
            skLineSegment(sketch, "E11.0.1.3", {"start": v(-34.49, 21.5) * mm, "end": v(-34.49, 16.47) * mm});
            skLineSegment(sketch, "E11.0.2.0", {"start": v(-34.49, 30.8) * mm, "end": v(-28.53, 30.8) * mm});
            skLineSegment(sketch, "E11.0.2.1", {"start": v(-28.53, 30.8) * mm, "end": v(-28.53, 25.77) * mm});
            skLineSegment(sketch, "E11.0.2.2", {"start": v(-34.49, 25.77) * mm, "end": v(-28.53, 25.77) * mm});
            skLineSegment(sketch, "E11.0.2.3", {"start": v(-34.49, 30.8) * mm, "end": v(-34.49, 25.77) * mm});
            skLineSegment(sketch, "E11.0.3.0", {"start": v(-34.49, 40.1) * mm, "end": v(-28.53, 40.1) * mm});
            skLineSegment(sketch, "E11.0.3.1", {"start": v(-28.53, 40.1) * mm, "end": v(-28.53, 35.07) * mm});
            skLineSegment(sketch, "E11.0.3.2", {"start": v(-34.49, 35.07) * mm, "end": v(-28.53, 35.07) * mm});
            skLineSegment(sketch, "E11.0.3.3", {"start": v(-34.49, 40.1) * mm, "end": v(-34.49, 35.07) * mm});
            skLineSegment(sketch, "E11.0.4.0", {"start": v(-34.49, 49.4) * mm, "end": v(-28.53, 49.4) * mm});
            skLineSegment(sketch, "E11.0.4.1", {"start": v(-28.53, 49.4) * mm, "end": v(-28.53, 44.37) * mm});
            skLineSegment(sketch, "E11.0.4.2", {"start": v(-34.49, 44.37) * mm, "end": v(-28.53, 44.37) * mm});
            skLineSegment(sketch, "E11.0.4.3", {"start": v(-34.49, 49.4) * mm, "end": v(-34.49, 44.37) * mm});
            skLineSegment(sketch, "E11.0.5.0", {"start": v(-34.49, 58.7) * mm, "end": v(-28.53, 58.7) * mm});
            skLineSegment(sketch, "E11.0.5.1", {"start": v(-28.53, 58.7) * mm, "end": v(-28.53, 53.67) * mm});
            skLineSegment(sketch, "E11.0.5.2", {"start": v(-34.49, 53.67) * mm, "end": v(-28.53, 53.67) * mm});
            skLineSegment(sketch, "E11.0.5.3", {"start": v(-34.49, 58.7) * mm, "end": v(-34.49, 53.67) * mm});
            skLineSegment(sketch, "E11.0.6.0", {"start": v(-34.49, 68) * mm, "end": v(-28.53, 68) * mm});
            skLineSegment(sketch, "E11.0.6.1", {"start": v(-28.53, 68) * mm, "end": v(-28.53, 62.97) * mm});
            skLineSegment(sketch, "E11.0.6.2", {"start": v(-34.49, 62.97) * mm, "end": v(-28.53, 62.97) * mm});
            skLineSegment(sketch, "E11.0.6.3", {"start": v(-34.49, 68) * mm, "end": v(-34.49, 62.97) * mm});
            skLineSegment(sketch, "E11.0.7.0", {"start": v(-34.49, 77.3) * mm, "end": v(-28.53, 77.3) * mm});
            skLineSegment(sketch, "E11.0.7.1", {"start": v(-28.53, 77.3) * mm, "end": v(-28.53, 72.27) * mm});
            skLineSegment(sketch, "E11.0.7.2", {"start": v(-34.49, 72.27) * mm, "end": v(-28.53, 72.27) * mm});
            skLineSegment(sketch, "E11.0.7.3", {"start": v(-34.49, 77.3) * mm, "end": v(-34.49, 72.27) * mm});
            skLineSegment(sketch, "E11.0.8.0", {"start": v(-34.49, 86.6) * mm, "end": v(-28.53, 86.6) * mm});
            skLineSegment(sketch, "E11.0.8.1", {"start": v(-28.53, 86.6) * mm, "end": v(-28.53, 81.57) * mm});
            skLineSegment(sketch, "E11.0.8.2", {"start": v(-34.49, 81.57) * mm, "end": v(-28.53, 81.57) * mm});
            skLineSegment(sketch, "E11.0.8.3", {"start": v(-34.49, 86.6) * mm, "end": v(-34.49, 81.57) * mm});
            skLineSegment(sketch, "E11.0.9.0", {"start": v(-34.49, 95.9) * mm, "end": v(-28.53, 95.9) * mm});
            skLineSegment(sketch, "E11.0.9.1", {"start": v(-28.53, 95.9) * mm, "end": v(-28.53, 90.87) * mm});
            skLineSegment(sketch, "E11.0.9.2", {"start": v(-34.49, 90.87) * mm, "end": v(-28.53, 90.87) * mm});
            skLineSegment(sketch, "E11.0.9.3", {"start": v(-34.49, 95.9) * mm, "end": v(-34.49, 90.87) * mm});
            skLineSegment(sketch, "E11.1.0.0", {"start": v(-25.96, 12.44) * mm, "end": v(-20, 12.44) * mm});
            skLineSegment(sketch, "E11.1.0.1", {"start": v(-20, 12.44) * mm, "end": v(-20, 7.4) * mm});
            skLineSegment(sketch, "E11.1.0.2", {"start": v(-25.96, 7.4) * mm, "end": v(-20, 7.4) * mm});
            skLineSegment(sketch, "E11.1.0.3", {"start": v(-25.96, 12.44) * mm, "end": v(-25.96, 7.4) * mm});
            skLineSegment(sketch, "E11.1.1.0", {"start": v(-25.96, 21.74) * mm, "end": v(-20, 21.74) * mm});
            skLineSegment(sketch, "E11.1.1.1", {"start": v(-20, 21.74) * mm, "end": v(-20, 16.7) * mm});
            skLineSegment(sketch, "E11.1.1.2", {"start": v(-25.96, 16.7) * mm, "end": v(-20, 16.7) * mm});
            skLineSegment(sketch, "E11.1.1.3", {"start": v(-25.96, 21.74) * mm, "end": v(-25.96, 16.7) * mm});
            skLineSegment(sketch, "E11.1.2.0", {"start": v(-25.96, 31.04) * mm, "end": v(-20, 31.04) * mm});
            skLineSegment(sketch, "E11.1.2.1", {"start": v(-20, 31.04) * mm, "end": v(-20, 26) * mm});
            skLineSegment(sketch, "E11.1.2.2", {"start": v(-25.96, 26) * mm, "end": v(-20, 26) * mm});
            skLineSegment(sketch, "E11.1.2.3", {"start": v(-25.96, 31.04) * mm, "end": v(-25.96, 26) * mm});
            skLineSegment(sketch, "E11.1.3.0", {"start": v(-25.96, 40.34) * mm, "end": v(-20, 40.34) * mm});
            skLineSegment(sketch, "E11.1.3.1", {"start": v(-20, 40.34) * mm, "end": v(-20, 35.3) * mm});
            skLineSegment(sketch, "E11.1.3.2", {"start": v(-25.96, 35.3) * mm, "end": v(-20, 35.3) * mm});
            skLineSegment(sketch, "E11.1.3.3", {"start": v(-25.96, 40.34) * mm, "end": v(-25.96, 35.3) * mm});
            skLineSegment(sketch, "E11.1.4.0", {"start": v(-25.96, 49.64) * mm, "end": v(-20, 49.64) * mm});
            skLineSegment(sketch, "E11.1.4.1", {"start": v(-20, 49.64) * mm, "end": v(-20, 44.6) * mm});
            skLineSegment(sketch, "E11.1.4.2", {"start": v(-25.96, 44.6) * mm, "end": v(-20, 44.6) * mm});
            skLineSegment(sketch, "E11.1.4.3", {"start": v(-25.96, 49.64) * mm, "end": v(-25.96, 44.6) * mm});
            skLineSegment(sketch, "E11.1.5.0", {"start": v(-25.96, 58.94) * mm, "end": v(-20, 58.94) * mm});
            skLineSegment(sketch, "E11.1.5.1", {"start": v(-20, 58.94) * mm, "end": v(-20, 53.9) * mm});
            skLineSegment(sketch, "E11.1.5.2", {"start": v(-25.96, 53.9) * mm, "end": v(-20, 53.9) * mm});
            skLineSegment(sketch, "E11.1.5.3", {"start": v(-25.96, 58.94) * mm, "end": v(-25.96, 53.9) * mm});
            skLineSegment(sketch, "E11.1.6.0", {"start": v(-25.96, 68.24) * mm, "end": v(-20, 68.24) * mm});
            skLineSegment(sketch, "E11.1.6.1", {"start": v(-20, 68.24) * mm, "end": v(-20, 63.2) * mm});
            skLineSegment(sketch, "E11.1.6.2", {"start": v(-25.96, 63.2) * mm, "end": v(-20, 63.2) * mm});
            skLineSegment(sketch, "E11.1.6.3", {"start": v(-25.96, 68.24) * mm, "end": v(-25.96, 63.2) * mm});
            skLineSegment(sketch, "E11.1.7.0", {"start": v(-25.96, 77.54) * mm, "end": v(-20, 77.54) * mm});
            skLineSegment(sketch, "E11.1.7.1", {"start": v(-20, 77.54) * mm, "end": v(-20, 72.5) * mm});
            skLineSegment(sketch, "E11.1.7.2", {"start": v(-25.96, 72.5) * mm, "end": v(-20, 72.5) * mm});
            skLineSegment(sketch, "E11.1.7.3", {"start": v(-25.96, 77.54) * mm, "end": v(-25.96, 72.5) * mm});
            skLineSegment(sketch, "E11.1.8.0", {"start": v(-25.96, 86.84) * mm, "end": v(-20, 86.84) * mm});
            skLineSegment(sketch, "E11.1.8.1", {"start": v(-20, 86.84) * mm, "end": v(-20, 81.8) * mm});
            skLineSegment(sketch, "E11.1.8.2", {"start": v(-25.96, 81.8) * mm, "end": v(-20, 81.8) * mm});
            skLineSegment(sketch, "E11.1.8.3", {"start": v(-25.96, 86.84) * mm, "end": v(-25.96, 81.8) * mm});
            skLineSegment(sketch, "E11.1.9.0", {"start": v(-25.96, 96.14) * mm, "end": v(-20, 96.14) * mm});
            skLineSegment(sketch, "E11.1.9.1", {"start": v(-20, 96.14) * mm, "end": v(-20, 91.1) * mm});
            skLineSegment(sketch, "E11.1.9.2", {"start": v(-25.96, 91.1) * mm, "end": v(-20, 91.1) * mm});
            skLineSegment(sketch, "E11.1.9.3", {"start": v(-25.96, 96.14) * mm, "end": v(-25.96, 91.1) * mm});
            skLineSegment(sketch, "E11.2.0.0", {"start": v(-17.43, 12.67) * mm, "end": v(-11.48, 12.67) * mm});
            skLineSegment(sketch, "E11.2.0.1", {"start": v(-11.48, 12.67) * mm, "end": v(-11.48, 7.64) * mm});
            skLineSegment(sketch, "E11.2.0.2", {"start": v(-17.43, 7.64) * mm, "end": v(-11.48, 7.64) * mm});
            skLineSegment(sketch, "E11.2.0.3", {"start": v(-17.43, 12.67) * mm, "end": v(-17.43, 7.64) * mm});
            skLineSegment(sketch, "E11.2.1.0", {"start": v(-17.43, 21.97) * mm, "end": v(-11.48, 21.97) * mm});
            skLineSegment(sketch, "E11.2.1.1", {"start": v(-11.48, 21.97) * mm, "end": v(-11.48, 16.94) * mm});
            skLineSegment(sketch, "E11.2.1.2", {"start": v(-17.43, 16.94) * mm, "end": v(-11.48, 16.94) * mm});
            skLineSegment(sketch, "E11.2.1.3", {"start": v(-17.43, 21.97) * mm, "end": v(-17.43, 16.94) * mm});
            skLineSegment(sketch, "E11.2.2.0", {"start": v(-17.43, 31.27) * mm, "end": v(-11.48, 31.27) * mm});
            skLineSegment(sketch, "E11.2.2.1", {"start": v(-11.48, 31.27) * mm, "end": v(-11.48, 26.24) * mm});
            skLineSegment(sketch, "E11.2.2.2", {"start": v(-17.43, 26.24) * mm, "end": v(-11.48, 26.24) * mm});
            skLineSegment(sketch, "E11.2.2.3", {"start": v(-17.43, 31.27) * mm, "end": v(-17.43, 26.24) * mm});
            skLineSegment(sketch, "E11.2.3.0", {"start": v(-17.43, 40.57) * mm, "end": v(-11.48, 40.57) * mm});
            skLineSegment(sketch, "E11.2.3.1", {"start": v(-11.48, 40.57) * mm, "end": v(-11.48, 35.54) * mm});
            skLineSegment(sketch, "E11.2.3.2", {"start": v(-17.43, 35.54) * mm, "end": v(-11.48, 35.54) * mm});
            skLineSegment(sketch, "E11.2.3.3", {"start": v(-17.43, 40.57) * mm, "end": v(-17.43, 35.54) * mm});
            skLineSegment(sketch, "E11.2.4.0", {"start": v(-17.43, 49.87) * mm, "end": v(-11.48, 49.87) * mm});
            skLineSegment(sketch, "E11.2.4.1", {"start": v(-11.48, 49.87) * mm, "end": v(-11.48, 44.84) * mm});
            skLineSegment(sketch, "E11.2.4.2", {"start": v(-17.43, 44.84) * mm, "end": v(-11.48, 44.84) * mm});
            skLineSegment(sketch, "E11.2.4.3", {"start": v(-17.43, 49.87) * mm, "end": v(-17.43, 44.84) * mm});
            skLineSegment(sketch, "E11.2.5.0", {"start": v(-17.43, 59.17) * mm, "end": v(-11.48, 59.17) * mm});
            skLineSegment(sketch, "E11.2.5.1", {"start": v(-11.48, 59.17) * mm, "end": v(-11.48, 54.14) * mm});
            skLineSegment(sketch, "E11.2.5.2", {"start": v(-17.43, 54.14) * mm, "end": v(-11.48, 54.14) * mm});
            skLineSegment(sketch, "E11.2.5.3", {"start": v(-17.43, 59.17) * mm, "end": v(-17.43, 54.14) * mm});
            skLineSegment(sketch, "E11.2.6.0", {"start": v(-17.43, 68.47) * mm, "end": v(-11.48, 68.47) * mm});
            skLineSegment(sketch, "E11.2.6.1", {"start": v(-11.48, 68.47) * mm, "end": v(-11.48, 63.44) * mm});
            skLineSegment(sketch, "E11.2.6.2", {"start": v(-17.43, 63.44) * mm, "end": v(-11.48, 63.44) * mm});
            skLineSegment(sketch, "E11.2.6.3", {"start": v(-17.43, 68.47) * mm, "end": v(-17.43, 63.44) * mm});
            skLineSegment(sketch, "E11.2.7.0", {"start": v(-17.43, 77.77) * mm, "end": v(-11.48, 77.77) * mm});
            skLineSegment(sketch, "E11.2.7.1", {"start": v(-11.48, 77.77) * mm, "end": v(-11.48, 72.74) * mm});
            skLineSegment(sketch, "E11.2.7.2", {"start": v(-17.43, 72.74) * mm, "end": v(-11.48, 72.74) * mm});
            skLineSegment(sketch, "E11.2.7.3", {"start": v(-17.43, 77.77) * mm, "end": v(-17.43, 72.74) * mm});
            skLineSegment(sketch, "E11.2.8.0", {"start": v(-17.43, 87.07) * mm, "end": v(-11.48, 87.07) * mm});
            skLineSegment(sketch, "E11.2.8.1", {"start": v(-11.48, 87.07) * mm, "end": v(-11.48, 82.04) * mm});
            skLineSegment(sketch, "E11.2.8.2", {"start": v(-17.43, 82.04) * mm, "end": v(-11.48, 82.04) * mm});
            skLineSegment(sketch, "E11.2.8.3", {"start": v(-17.43, 87.07) * mm, "end": v(-17.43, 82.04) * mm});
            skLineSegment(sketch, "E11.2.9.0", {"start": v(-17.43, 96.37) * mm, "end": v(-11.48, 96.37) * mm});
            skLineSegment(sketch, "E11.2.9.1", {"start": v(-11.48, 96.37) * mm, "end": v(-11.48, 91.34) * mm});
            skLineSegment(sketch, "E11.2.9.2", {"start": v(-17.43, 91.34) * mm, "end": v(-11.48, 91.34) * mm});
            skLineSegment(sketch, "E11.2.9.3", {"start": v(-17.43, 96.37) * mm, "end": v(-17.43, 91.34) * mm});
            skLineSegment(sketch, "E11.3.0.0", {"start": v(-8.9, 12.9) * mm, "end": v(-2.95, 12.9) * mm});
            skLineSegment(sketch, "E11.3.0.1", {"start": v(-2.95, 12.9) * mm, "end": v(-2.95, 7.87) * mm});
            skLineSegment(sketch, "E11.3.0.2", {"start": v(-8.9, 7.87) * mm, "end": v(-2.95, 7.87) * mm});
            skLineSegment(sketch, "E11.3.0.3", {"start": v(-8.9, 12.9) * mm, "end": v(-8.9, 7.87) * mm});
            skLineSegment(sketch, "E11.3.1.0", {"start": v(-8.9, 22.2) * mm, "end": v(-2.95, 22.2) * mm});
            skLineSegment(sketch, "E11.3.1.1", {"start": v(-2.95, 22.2) * mm, "end": v(-2.95, 17.17) * mm});
            skLineSegment(sketch, "E11.3.1.2", {"start": v(-8.9, 17.17) * mm, "end": v(-2.95, 17.17) * mm});
            skLineSegment(sketch, "E11.3.1.3", {"start": v(-8.9, 22.2) * mm, "end": v(-8.9, 17.17) * mm});
            skLineSegment(sketch, "E11.3.2.0", {"start": v(-8.9, 31.5) * mm, "end": v(-2.95, 31.5) * mm});
            skLineSegment(sketch, "E11.3.2.1", {"start": v(-2.95, 31.5) * mm, "end": v(-2.95, 26.47) * mm});
            skLineSegment(sketch, "E11.3.2.2", {"start": v(-8.9, 26.47) * mm, "end": v(-2.95, 26.47) * mm});
            skLineSegment(sketch, "E11.3.2.3", {"start": v(-8.9, 31.5) * mm, "end": v(-8.9, 26.47) * mm});
            skLineSegment(sketch, "E11.3.3.0", {"start": v(-8.9, 40.8) * mm, "end": v(-2.95, 40.8) * mm});
            skLineSegment(sketch, "E11.3.3.1", {"start": v(-2.95, 40.8) * mm, "end": v(-2.95, 35.77) * mm});
            skLineSegment(sketch, "E11.3.3.2", {"start": v(-8.9, 35.77) * mm, "end": v(-2.95, 35.77) * mm});
            skLineSegment(sketch, "E11.3.3.3", {"start": v(-8.9, 40.8) * mm, "end": v(-8.9, 35.77) * mm});
            skLineSegment(sketch, "E11.3.4.0", {"start": v(-8.9, 50.1) * mm, "end": v(-2.95, 50.1) * mm});
            skLineSegment(sketch, "E11.3.4.1", {"start": v(-2.95, 50.1) * mm, "end": v(-2.95, 45.07) * mm});
            skLineSegment(sketch, "E11.3.4.2", {"start": v(-8.9, 45.07) * mm, "end": v(-2.95, 45.07) * mm});
            skLineSegment(sketch, "E11.3.4.3", {"start": v(-8.9, 50.1) * mm, "end": v(-8.9, 45.07) * mm});
            skLineSegment(sketch, "E11.3.5.0", {"start": v(-8.9, 59.4) * mm, "end": v(-2.95, 59.4) * mm});
            skLineSegment(sketch, "E11.3.5.1", {"start": v(-2.95, 59.4) * mm, "end": v(-2.95, 54.37) * mm});
            skLineSegment(sketch, "E11.3.5.2", {"start": v(-8.9, 54.37) * mm, "end": v(-2.95, 54.37) * mm});
            skLineSegment(sketch, "E11.3.5.3", {"start": v(-8.9, 59.4) * mm, "end": v(-8.9, 54.37) * mm});
            skLineSegment(sketch, "E11.3.6.0", {"start": v(-8.9, 68.7) * mm, "end": v(-2.95, 68.7) * mm});
            skLineSegment(sketch, "E11.3.6.1", {"start": v(-2.95, 68.7) * mm, "end": v(-2.95, 63.67) * mm});
            skLineSegment(sketch, "E11.3.6.2", {"start": v(-8.9, 63.67) * mm, "end": v(-2.95, 63.67) * mm});
            skLineSegment(sketch, "E11.3.6.3", {"start": v(-8.9, 68.7) * mm, "end": v(-8.9, 63.67) * mm});
            skLineSegment(sketch, "E11.3.7.0", {"start": v(-8.9, 78) * mm, "end": v(-2.95, 78) * mm});
            skLineSegment(sketch, "E11.3.7.1", {"start": v(-2.95, 78) * mm, "end": v(-2.95, 72.97) * mm});
            skLineSegment(sketch, "E11.3.7.2", {"start": v(-8.9, 72.97) * mm, "end": v(-2.95, 72.97) * mm});
            skLineSegment(sketch, "E11.3.7.3", {"start": v(-8.9, 78) * mm, "end": v(-8.9, 72.97) * mm});
            skLineSegment(sketch, "E11.3.8.0", {"start": v(-8.9, 87.3) * mm, "end": v(-2.95, 87.3) * mm});
            skLineSegment(sketch, "E11.3.8.1", {"start": v(-2.95, 87.3) * mm, "end": v(-2.95, 82.27) * mm});
            skLineSegment(sketch, "E11.3.8.2", {"start": v(-8.9, 82.27) * mm, "end": v(-2.95, 82.27) * mm});
            skLineSegment(sketch, "E11.3.8.3", {"start": v(-8.9, 87.3) * mm, "end": v(-8.9, 82.27) * mm});
            skLineSegment(sketch, "E11.3.9.0", {"start": v(-8.9, 96.6) * mm, "end": v(-2.95, 96.6) * mm});
            skLineSegment(sketch, "E11.3.9.1", {"start": v(-2.95, 96.6) * mm, "end": v(-2.95, 91.57) * mm});
            skLineSegment(sketch, "E11.3.9.2", {"start": v(-8.9, 91.57) * mm, "end": v(-2.95, 91.57) * mm});
            skLineSegment(sketch, "E11.3.9.3", {"start": v(-8.9, 96.6) * mm, "end": v(-8.9, 91.57) * mm});
            skLineSegment(sketch, "E11.4.0.0", {"start": v(-0.37, 13.14) * mm, "end": v(5.58, 13.14) * mm});
            skLineSegment(sketch, "E11.4.0.1", {"start": v(5.58, 13.14) * mm, "end": v(5.58, 8.1) * mm});
            skLineSegment(sketch, "E11.4.0.2", {"start": v(-0.37, 8.1) * mm, "end": v(5.58, 8.1) * mm});
            skLineSegment(sketch, "E11.4.0.3", {"start": v(-0.37, 13.14) * mm, "end": v(-0.37, 8.1) * mm});
            skLineSegment(sketch, "E11.4.1.0", {"start": v(-0.37, 22.44) * mm, "end": v(5.58, 22.44) * mm});
            skLineSegment(sketch, "E11.4.1.1", {"start": v(5.58, 22.44) * mm, "end": v(5.58, 17.4) * mm});
            skLineSegment(sketch, "E11.4.1.2", {"start": v(-0.37, 17.4) * mm, "end": v(5.58, 17.4) * mm});
            skLineSegment(sketch, "E11.4.1.3", {"start": v(-0.37, 22.44) * mm, "end": v(-0.37, 17.4) * mm});
            skLineSegment(sketch, "E11.4.2.0", {"start": v(-0.37, 31.74) * mm, "end": v(5.58, 31.74) * mm});
            skLineSegment(sketch, "E11.4.2.1", {"start": v(5.58, 31.74) * mm, "end": v(5.58, 26.7) * mm});
            skLineSegment(sketch, "E11.4.2.2", {"start": v(-0.37, 26.7) * mm, "end": v(5.58, 26.7) * mm});
            skLineSegment(sketch, "E11.4.2.3", {"start": v(-0.37, 31.74) * mm, "end": v(-0.37, 26.7) * mm});
            skLineSegment(sketch, "E11.4.3.0", {"start": v(-0.37, 41.04) * mm, "end": v(5.58, 41.04) * mm});
            skLineSegment(sketch, "E11.4.3.1", {"start": v(5.58, 41.04) * mm, "end": v(5.58, 36) * mm});
            skLineSegment(sketch, "E11.4.3.2", {"start": v(-0.37, 36) * mm, "end": v(5.58, 36) * mm});
            skLineSegment(sketch, "E11.4.3.3", {"start": v(-0.37, 41.04) * mm, "end": v(-0.37, 36) * mm});
            skLineSegment(sketch, "E11.4.4.0", {"start": v(-0.37, 50.34) * mm, "end": v(5.58, 50.34) * mm});
            skLineSegment(sketch, "E11.4.4.1", {"start": v(5.58, 50.34) * mm, "end": v(5.58, 45.3) * mm});
            skLineSegment(sketch, "E11.4.4.2", {"start": v(-0.37, 45.3) * mm, "end": v(5.58, 45.3) * mm});
            skLineSegment(sketch, "E11.4.4.3", {"start": v(-0.37, 50.34) * mm, "end": v(-0.37, 45.3) * mm});
            skLineSegment(sketch, "E11.4.5.0", {"start": v(-0.37, 59.64) * mm, "end": v(5.58, 59.64) * mm});
            skLineSegment(sketch, "E11.4.5.1", {"start": v(5.58, 59.64) * mm, "end": v(5.58, 54.6) * mm});
            skLineSegment(sketch, "E11.4.5.2", {"start": v(-0.37, 54.6) * mm, "end": v(5.58, 54.6) * mm});
            skLineSegment(sketch, "E11.4.5.3", {"start": v(-0.37, 59.64) * mm, "end": v(-0.37, 54.6) * mm});
            skLineSegment(sketch, "E11.4.6.0", {"start": v(-0.37, 68.94) * mm, "end": v(5.58, 68.94) * mm});
            skLineSegment(sketch, "E11.4.6.1", {"start": v(5.58, 68.94) * mm, "end": v(5.58, 63.9) * mm});
            skLineSegment(sketch, "E11.4.6.2", {"start": v(-0.37, 63.9) * mm, "end": v(5.58, 63.9) * mm});
            skLineSegment(sketch, "E11.4.6.3", {"start": v(-0.37, 68.94) * mm, "end": v(-0.37, 63.9) * mm});
            skLineSegment(sketch, "E11.4.7.0", {"start": v(-0.37, 78.24) * mm, "end": v(5.58, 78.24) * mm});
            skLineSegment(sketch, "E11.4.7.1", {"start": v(5.58, 78.24) * mm, "end": v(5.58, 73.2) * mm});
            skLineSegment(sketch, "E11.4.7.2", {"start": v(-0.37, 73.2) * mm, "end": v(5.58, 73.2) * mm});
            skLineSegment(sketch, "E11.4.7.3", {"start": v(-0.37, 78.24) * mm, "end": v(-0.37, 73.2) * mm});
            skLineSegment(sketch, "E11.4.8.0", {"start": v(-0.37, 87.54) * mm, "end": v(5.58, 87.54) * mm});
            skLineSegment(sketch, "E11.4.8.1", {"start": v(5.58, 87.54) * mm, "end": v(5.58, 82.5) * mm});
            skLineSegment(sketch, "E11.4.8.2", {"start": v(-0.37, 82.5) * mm, "end": v(5.58, 82.5) * mm});
            skLineSegment(sketch, "E11.4.8.3", {"start": v(-0.37, 87.54) * mm, "end": v(-0.37, 82.5) * mm});
            skLineSegment(sketch, "E11.4.9.0", {"start": v(-0.37, 96.84) * mm, "end": v(5.58, 96.84) * mm});
            skLineSegment(sketch, "E11.4.9.1", {"start": v(5.58, 96.84) * mm, "end": v(5.58, 91.8) * mm});
            skLineSegment(sketch, "E11.4.9.2", {"start": v(-0.37, 91.8) * mm, "end": v(5.58, 91.8) * mm});
            skLineSegment(sketch, "E11.4.9.3", {"start": v(-0.37, 96.84) * mm, "end": v(-0.37, 91.8) * mm});
            skLineSegment(sketch, "E11.direction1", {"start": v(-34.49, 12.2) * mm, "end": v(-25.96, 12.44) * mm, "construction": true});
            skLineSegment(sketch, "E11.direction2", {"start": v(-34.49, 12.2) * mm, "end": v(-34.49, 21.5) * mm, "construction": true});
            skLineSegment(sketch, "E12.0.0.10", {"start": v(-34.49, 105.2) * mm, "end": v(-28.53, 105.2) * mm});
            skLineSegment(sketch, "E12.3.0.10", {"start": v(-28.53, 105.2) * mm, "end": v(-28.53, 100.17) * mm});
            skLineSegment(sketch, "E12.6.0.10", {"start": v(-34.49, 100.17) * mm, "end": v(-28.53, 100.17) * mm});
            skLineSegment(sketch, "E12.9.0.10", {"start": v(-34.49, 105.2) * mm, "end": v(-34.49, 100.17) * mm});
            skLineSegment(sketch, "E12.0.0.11", {"start": v(-34.49, 114.5) * mm, "end": v(-28.53, 114.5) * mm});
            skLineSegment(sketch, "E12.3.0.11", {"start": v(-28.53, 114.5) * mm, "end": v(-28.53, 109.47) * mm});
            skLineSegment(sketch, "E12.6.0.11", {"start": v(-34.49, 109.47) * mm, "end": v(-28.53, 109.47) * mm});
            skLineSegment(sketch, "E12.9.0.11", {"start": v(-34.49, 114.5) * mm, "end": v(-34.49, 109.47) * mm});
            skLineSegment(sketch, "E12.0.0.12", {"start": v(-34.49, 123.8) * mm, "end": v(-28.53, 123.8) * mm});
            skLineSegment(sketch, "E12.3.0.12", {"start": v(-28.53, 123.8) * mm, "end": v(-28.53, 118.77) * mm});
            skLineSegment(sketch, "E12.6.0.12", {"start": v(-34.49, 118.77) * mm, "end": v(-28.53, 118.77) * mm});
            skLineSegment(sketch, "E12.9.0.12", {"start": v(-34.49, 123.8) * mm, "end": v(-34.49, 118.77) * mm});
            skLineSegment(sketch, "E12.0.0.13", {"start": v(-34.49, 133.1) * mm, "end": v(-28.53, 133.1) * mm});
            skLineSegment(sketch, "E12.3.0.13", {"start": v(-28.53, 133.1) * mm, "end": v(-28.53, 128.07) * mm});
            skLineSegment(sketch, "E12.6.0.13", {"start": v(-34.49, 128.07) * mm, "end": v(-28.53, 128.07) * mm});
            skLineSegment(sketch, "E12.9.0.13", {"start": v(-34.49, 133.1) * mm, "end": v(-34.49, 128.07) * mm});
            skLineSegment(sketch, "E12.0.0.14", {"start": v(-34.49, 142.4) * mm, "end": v(-28.53, 142.4) * mm});
            skLineSegment(sketch, "E12.3.0.14", {"start": v(-28.53, 142.4) * mm, "end": v(-28.53, 137.37) * mm});
            skLineSegment(sketch, "E12.6.0.14", {"start": v(-34.49, 137.37) * mm, "end": v(-28.53, 137.37) * mm});
            skLineSegment(sketch, "E12.9.0.14", {"start": v(-34.49, 142.4) * mm, "end": v(-34.49, 137.37) * mm});
            skLineSegment(sketch, "E12.0.1.10", {"start": v(-25.96, 105.44) * mm, "end": v(-20, 105.44) * mm});
            skLineSegment(sketch, "E12.3.1.10", {"start": v(-20, 105.44) * mm, "end": v(-20, 100.4) * mm});
            skLineSegment(sketch, "E12.6.1.10", {"start": v(-25.96, 100.4) * mm, "end": v(-20, 100.4) * mm});
            skLineSegment(sketch, "E12.9.1.10", {"start": v(-25.96, 105.44) * mm, "end": v(-25.96, 100.4) * mm});
            skLineSegment(sketch, "E12.0.1.11", {"start": v(-25.96, 114.74) * mm, "end": v(-20, 114.74) * mm});
            skLineSegment(sketch, "E12.3.1.11", {"start": v(-20, 114.74) * mm, "end": v(-20, 109.7) * mm});
            skLineSegment(sketch, "E12.6.1.11", {"start": v(-25.96, 109.7) * mm, "end": v(-20, 109.7) * mm});
            skLineSegment(sketch, "E12.9.1.11", {"start": v(-25.96, 114.74) * mm, "end": v(-25.96, 109.7) * mm});
            skLineSegment(sketch, "E12.0.1.12", {"start": v(-25.96, 124.04) * mm, "end": v(-20, 124.04) * mm});
            skLineSegment(sketch, "E12.3.1.12", {"start": v(-20, 124.04) * mm, "end": v(-20, 119) * mm});
            skLineSegment(sketch, "E12.6.1.12", {"start": v(-25.96, 119) * mm, "end": v(-20, 119) * mm});
            skLineSegment(sketch, "E12.9.1.12", {"start": v(-25.96, 124.04) * mm, "end": v(-25.96, 119) * mm});
            skLineSegment(sketch, "E12.0.1.13", {"start": v(-25.96, 133.34) * mm, "end": v(-20, 133.34) * mm});
            skLineSegment(sketch, "E12.3.1.13", {"start": v(-20, 133.34) * mm, "end": v(-20, 128.3) * mm});
            skLineSegment(sketch, "E12.6.1.13", {"start": v(-25.96, 128.3) * mm, "end": v(-20, 128.3) * mm});
            skLineSegment(sketch, "E12.9.1.13", {"start": v(-25.96, 133.34) * mm, "end": v(-25.96, 128.3) * mm});
            skLineSegment(sketch, "E12.0.1.14", {"start": v(-25.96, 142.64) * mm, "end": v(-20, 142.64) * mm});
            skLineSegment(sketch, "E12.3.1.14", {"start": v(-20, 142.64) * mm, "end": v(-20, 137.6) * mm});
            skLineSegment(sketch, "E12.6.1.14", {"start": v(-25.96, 137.6) * mm, "end": v(-20, 137.6) * mm});
            skLineSegment(sketch, "E12.9.1.14", {"start": v(-25.96, 142.64) * mm, "end": v(-25.96, 137.6) * mm});
            skLineSegment(sketch, "E12.0.2.10", {"start": v(-17.43, 105.67) * mm, "end": v(-11.48, 105.67) * mm});
            skLineSegment(sketch, "E12.3.2.10", {"start": v(-11.48, 105.67) * mm, "end": v(-11.48, 100.64) * mm});
            skLineSegment(sketch, "E12.6.2.10", {"start": v(-17.43, 100.64) * mm, "end": v(-11.48, 100.64) * mm});
            skLineSegment(sketch, "E12.9.2.10", {"start": v(-17.43, 105.67) * mm, "end": v(-17.43, 100.64) * mm});
            skLineSegment(sketch, "E12.0.2.11", {"start": v(-17.43, 114.97) * mm, "end": v(-11.48, 114.97) * mm});
            skLineSegment(sketch, "E12.3.2.11", {"start": v(-11.48, 114.97) * mm, "end": v(-11.48, 109.94) * mm});
            skLineSegment(sketch, "E12.6.2.11", {"start": v(-17.43, 109.94) * mm, "end": v(-11.48, 109.94) * mm});
            skLineSegment(sketch, "E12.9.2.11", {"start": v(-17.43, 114.97) * mm, "end": v(-17.43, 109.94) * mm});
            skLineSegment(sketch, "E12.0.2.12", {"start": v(-17.43, 124.27) * mm, "end": v(-11.48, 124.27) * mm});
            skLineSegment(sketch, "E12.3.2.12", {"start": v(-11.48, 124.27) * mm, "end": v(-11.48, 119.24) * mm});
            skLineSegment(sketch, "E12.6.2.12", {"start": v(-17.43, 119.24) * mm, "end": v(-11.48, 119.24) * mm});
            skLineSegment(sketch, "E12.9.2.12", {"start": v(-17.43, 124.27) * mm, "end": v(-17.43, 119.24) * mm});
            skLineSegment(sketch, "E12.0.2.13", {"start": v(-17.43, 133.57) * mm, "end": v(-11.48, 133.57) * mm});
            skLineSegment(sketch, "E12.3.2.13", {"start": v(-11.48, 133.57) * mm, "end": v(-11.48, 128.54) * mm});
            skLineSegment(sketch, "E12.6.2.13", {"start": v(-17.43, 128.54) * mm, "end": v(-11.48, 128.54) * mm});
            skLineSegment(sketch, "E12.9.2.13", {"start": v(-17.43, 133.57) * mm, "end": v(-17.43, 128.54) * mm});
            skLineSegment(sketch, "E12.0.2.14", {"start": v(-17.43, 142.87) * mm, "end": v(-11.48, 142.87) * mm});
            skLineSegment(sketch, "E12.3.2.14", {"start": v(-11.48, 142.87) * mm, "end": v(-11.48, 137.84) * mm});
            skLineSegment(sketch, "E12.6.2.14", {"start": v(-17.43, 137.84) * mm, "end": v(-11.48, 137.84) * mm});
            skLineSegment(sketch, "E12.9.2.14", {"start": v(-17.43, 142.87) * mm, "end": v(-17.43, 137.84) * mm});
            skLineSegment(sketch, "E12.0.3.10", {"start": v(-8.9, 105.9) * mm, "end": v(-2.95, 105.9) * mm});
            skLineSegment(sketch, "E12.3.3.10", {"start": v(-2.95, 105.9) * mm, "end": v(-2.95, 100.87) * mm});
            skLineSegment(sketch, "E12.6.3.10", {"start": v(-8.9, 100.87) * mm, "end": v(-2.95, 100.87) * mm});
            skLineSegment(sketch, "E12.9.3.10", {"start": v(-8.9, 105.9) * mm, "end": v(-8.9, 100.87) * mm});
            skLineSegment(sketch, "E12.0.3.11", {"start": v(-8.9, 115.2) * mm, "end": v(-2.95, 115.2) * mm});
            skLineSegment(sketch, "E12.3.3.11", {"start": v(-2.95, 115.2) * mm, "end": v(-2.95, 110.17) * mm});
            skLineSegment(sketch, "E12.6.3.11", {"start": v(-8.9, 110.17) * mm, "end": v(-2.95, 110.17) * mm});
            skLineSegment(sketch, "E12.9.3.11", {"start": v(-8.9, 115.2) * mm, "end": v(-8.9, 110.17) * mm});
            skLineSegment(sketch, "E12.0.3.12", {"start": v(-8.9, 124.5) * mm, "end": v(-2.95, 124.5) * mm});
            skLineSegment(sketch, "E12.3.3.12", {"start": v(-2.95, 124.5) * mm, "end": v(-2.95, 119.47) * mm});
            skLineSegment(sketch, "E12.6.3.12", {"start": v(-8.9, 119.47) * mm, "end": v(-2.95, 119.47) * mm});
            skLineSegment(sketch, "E12.9.3.12", {"start": v(-8.9, 124.5) * mm, "end": v(-8.9, 119.47) * mm});
            skLineSegment(sketch, "E12.0.3.13", {"start": v(-8.9, 133.8) * mm, "end": v(-2.95, 133.8) * mm});
            skLineSegment(sketch, "E12.3.3.13", {"start": v(-2.95, 133.8) * mm, "end": v(-2.95, 128.77) * mm});
            skLineSegment(sketch, "E12.6.3.13", {"start": v(-8.9, 128.77) * mm, "end": v(-2.95, 128.77) * mm});
            skLineSegment(sketch, "E12.9.3.13", {"start": v(-8.9, 133.8) * mm, "end": v(-8.9, 128.77) * mm});
            skLineSegment(sketch, "E12.0.3.14", {"start": v(-8.9, 143.1) * mm, "end": v(-2.95, 143.1) * mm});
            skLineSegment(sketch, "E12.3.3.14", {"start": v(-2.95, 143.1) * mm, "end": v(-2.95, 138.07) * mm});
            skLineSegment(sketch, "E12.6.3.14", {"start": v(-8.9, 138.07) * mm, "end": v(-2.95, 138.07) * mm});
            skLineSegment(sketch, "E12.9.3.14", {"start": v(-8.9, 143.1) * mm, "end": v(-8.9, 138.07) * mm});
            skLineSegment(sketch, "E12.0.4.10", {"start": v(-0.37, 106.14) * mm, "end": v(5.58, 106.14) * mm});
            skLineSegment(sketch, "E12.3.4.10", {"start": v(5.58, 106.14) * mm, "end": v(5.58, 101.1) * mm});
            skLineSegment(sketch, "E12.6.4.10", {"start": v(-0.37, 101.1) * mm, "end": v(5.58, 101.1) * mm});
            skLineSegment(sketch, "E12.9.4.10", {"start": v(-0.37, 106.14) * mm, "end": v(-0.37, 101.1) * mm});
            skLineSegment(sketch, "E12.0.4.11", {"start": v(-0.37, 115.44) * mm, "end": v(5.58, 115.44) * mm});
            skLineSegment(sketch, "E12.3.4.11", {"start": v(5.58, 115.44) * mm, "end": v(5.58, 110.4) * mm});
            skLineSegment(sketch, "E12.6.4.11", {"start": v(-0.37, 110.4) * mm, "end": v(5.58, 110.4) * mm});
            skLineSegment(sketch, "E12.9.4.11", {"start": v(-0.37, 115.44) * mm, "end": v(-0.37, 110.4) * mm});
            skLineSegment(sketch, "E12.0.4.12", {"start": v(-0.37, 124.74) * mm, "end": v(5.58, 124.74) * mm});
            skLineSegment(sketch, "E12.3.4.12", {"start": v(5.58, 124.74) * mm, "end": v(5.58, 119.7) * mm});
            skLineSegment(sketch, "E12.6.4.12", {"start": v(-0.37, 119.7) * mm, "end": v(5.58, 119.7) * mm});
            skLineSegment(sketch, "E12.9.4.12", {"start": v(-0.37, 124.74) * mm, "end": v(-0.37, 119.7) * mm});
            skLineSegment(sketch, "E12.0.4.13", {"start": v(-0.37, 134.04) * mm, "end": v(5.58, 134.04) * mm});
            skLineSegment(sketch, "E12.3.4.13", {"start": v(5.58, 134.04) * mm, "end": v(5.58, 129) * mm});
            skLineSegment(sketch, "E12.6.4.13", {"start": v(-0.37, 129) * mm, "end": v(5.58, 129) * mm});
            skLineSegment(sketch, "E12.9.4.13", {"start": v(-0.37, 134.04) * mm, "end": v(-0.37, 129) * mm});
            skLineSegment(sketch, "E12.0.4.14", {"start": v(-0.37, 143.34) * mm, "end": v(5.58, 143.34) * mm});
            skLineSegment(sketch, "E12.3.4.14", {"start": v(5.58, 143.34) * mm, "end": v(5.58, 138.3) * mm});
            skLineSegment(sketch, "E12.6.4.14", {"start": v(-0.37, 138.3) * mm, "end": v(5.58, 138.3) * mm});
            skLineSegment(sketch, "E12.9.4.14", {"start": v(-0.37, 143.34) * mm, "end": v(-0.37, 138.3) * mm});
            skLineSegment(sketch, "E13.0.0.15", {"start": v(-34.49, 151.7) * mm, "end": v(-28.53, 151.7) * mm});
            skLineSegment(sketch, "E13.3.0.15", {"start": v(-28.53, 151.7) * mm, "end": v(-28.53, 146.67) * mm});
            skLineSegment(sketch, "E13.6.0.15", {"start": v(-34.49, 146.67) * mm, "end": v(-28.53, 146.67) * mm});
            skLineSegment(sketch, "E13.9.0.15", {"start": v(-34.49, 151.7) * mm, "end": v(-34.49, 146.67) * mm});
            skLineSegment(sketch, "E13.0.1.15", {"start": v(-25.96, 151.94) * mm, "end": v(-20, 151.94) * mm});
            skLineSegment(sketch, "E13.3.1.15", {"start": v(-20, 151.94) * mm, "end": v(-20, 146.9) * mm});
            skLineSegment(sketch, "E13.6.1.15", {"start": v(-25.96, 146.9) * mm, "end": v(-20, 146.9) * mm});
            skLineSegment(sketch, "E13.9.1.15", {"start": v(-25.96, 151.94) * mm, "end": v(-25.96, 146.9) * mm});
            skLineSegment(sketch, "E13.0.2.15", {"start": v(-17.43, 152.17) * mm, "end": v(-11.48, 152.17) * mm});
            skLineSegment(sketch, "E13.3.2.15", {"start": v(-11.48, 152.17) * mm, "end": v(-11.48, 147.14) * mm});
            skLineSegment(sketch, "E13.6.2.15", {"start": v(-17.43, 147.14) * mm, "end": v(-11.48, 147.14) * mm});
            skLineSegment(sketch, "E13.9.2.15", {"start": v(-17.43, 152.17) * mm, "end": v(-17.43, 147.14) * mm});
            skLineSegment(sketch, "E13.0.3.15", {"start": v(-8.9, 152.4) * mm, "end": v(-2.95, 152.4) * mm});
            skLineSegment(sketch, "E13.3.3.15", {"start": v(-2.95, 152.4) * mm, "end": v(-2.95, 147.37) * mm});
            skLineSegment(sketch, "E13.6.3.15", {"start": v(-8.9, 147.37) * mm, "end": v(-2.95, 147.37) * mm});
            skLineSegment(sketch, "E13.9.3.15", {"start": v(-8.9, 152.4) * mm, "end": v(-8.9, 147.37) * mm});
            skLineSegment(sketch, "E13.0.4.15", {"start": v(-0.37, 152.64) * mm, "end": v(5.58, 152.64) * mm});
            skLineSegment(sketch, "E13.3.4.15", {"start": v(5.58, 152.64) * mm, "end": v(5.58, 147.6) * mm});
            skLineSegment(sketch, "E13.6.4.15", {"start": v(-0.37, 147.6) * mm, "end": v(5.58, 147.6) * mm});
            skLineSegment(sketch, "E13.9.4.15", {"start": v(-0.37, 152.64) * mm, "end": v(-0.37, 147.6) * mm});
            skSolve(sketch);
        }
        {
            var Q0;
            Q0 = qSketchRegion(id + "F14", true);
            extrude(context, id + "F15", {"entities" : qUnion([Q0]), "operationType" : NewBodyOperationType.REMOVE, "endBound" : BoundingType.THROUGH_ALL, "oppositeDirection" : true, "depth" : 25 * mm});
        }
        {
            var Q0;
            Q0=makeQuery(id+"F5.opExtrude","SWEPT_FACE",FACE,{"disambiguationData":[OSD([sQuery(id+"F4.wireOp",EDGE,"E2.top")])]});
            var sketch = newSketch(context, id + "F16", { "sketchPlane" : qUnion([Q0])});
            skLineSegment(sketch, "E14.top", {"start": v(-41.78, 160.12) * mm, "end": v(-36.91, 160.12) * mm});
            skLineSegment(sketch, "E14.left", {"start": v(-41.78, 166) * mm, "end": v(-41.78, 160.12) * mm});
            skLineSegment(sketch, "E14.right", {"start": v(-36.91, 166) * mm, "end": v(-36.91, 160.12) * mm});
            skArc(sketch, "E15", {"start": v(-36.91, 166) * mm, "mid": v(-39.35, 168.43) * mm, "end": v(-41.78, 166) * mm});
            skLineSegment(sketch, "E16.0.1.0", {"start": v(-41.8, 169.9) * mm, "end": v(-36.93, 169.9) * mm});
            skLineSegment(sketch, "E16.0.1.1", {"start": v(-36.93, 175.77) * mm, "end": v(-36.93, 169.9) * mm});
            skArc(sketch, "E16.0.1.2", {"start": v(-36.93, 175.77) * mm, "mid": v(-39.37, 178.2) * mm, "end": v(-41.8, 175.77) * mm});
            skLineSegment(sketch, "E16.0.1.3", {"start": v(-41.8, 175.77) * mm, "end": v(-41.8, 169.9) * mm});
            skLineSegment(sketch, "E16.0.2.0", {"start": v(-41.82, 179.68) * mm, "end": v(-36.95, 179.68) * mm});
            skLineSegment(sketch, "E16.0.2.1", {"start": v(-36.95, 185.55) * mm, "end": v(-36.95, 179.68) * mm});
            skArc(sketch, "E16.0.2.2", {"start": v(-36.95, 185.55) * mm, "mid": v(-39.38, 187.98) * mm, "end": v(-41.82, 185.55) * mm});
            skLineSegment(sketch, "E16.0.2.3", {"start": v(-41.82, 185.55) * mm, "end": v(-41.82, 179.68) * mm});
            skLineSegment(sketch, "E16.0.3.0", {"start": v(-41.83, 189.45) * mm, "end": v(-36.96, 189.45) * mm});
            skLineSegment(sketch, "E16.0.3.1", {"start": v(-36.96, 195.32) * mm, "end": v(-36.96, 189.45) * mm});
            skArc(sketch, "E16.0.3.2", {"start": v(-36.96, 195.32) * mm, "mid": v(-39.4, 197.76) * mm, "end": v(-41.83, 195.32) * mm});
            skLineSegment(sketch, "E16.0.3.3", {"start": v(-41.83, 195.32) * mm, "end": v(-41.83, 189.45) * mm});
            skLineSegment(sketch, "E16.1.0.0", {"start": v(-31.3, 160.2) * mm, "end": v(-26.43, 160.2) * mm});
            skLineSegment(sketch, "E16.1.0.1", {"start": v(-26.43, 166.07) * mm, "end": v(-26.43, 160.2) * mm});
            skArc(sketch, "E16.1.0.2", {"start": v(-26.43, 166.07) * mm, "mid": v(-28.87, 168.5) * mm, "end": v(-31.3, 166.07) * mm});
            skLineSegment(sketch, "E16.1.0.3", {"start": v(-31.3, 166.07) * mm, "end": v(-31.3, 160.2) * mm});
            skLineSegment(sketch, "E16.1.1.0", {"start": v(-31.32, 169.98) * mm, "end": v(-26.45, 169.98) * mm});
            skLineSegment(sketch, "E16.1.1.1", {"start": v(-26.45, 175.85) * mm, "end": v(-26.45, 169.98) * mm});
            skArc(sketch, "E16.1.1.2", {"start": v(-26.45, 175.85) * mm, "mid": v(-28.88, 178.28) * mm, "end": v(-31.32, 175.85) * mm});
            skLineSegment(sketch, "E16.1.1.3", {"start": v(-31.32, 175.85) * mm, "end": v(-31.32, 169.98) * mm});
            skLineSegment(sketch, "E16.1.2.0", {"start": v(-31.33, 179.75) * mm, "end": v(-26.46, 179.75) * mm});
            skLineSegment(sketch, "E16.1.2.1", {"start": v(-26.46, 185.62) * mm, "end": v(-26.46, 179.75) * mm});
            skArc(sketch, "E16.1.2.2", {"start": v(-26.46, 185.62) * mm, "mid": v(-28.9, 188.06) * mm, "end": v(-31.33, 185.62) * mm});
            skLineSegment(sketch, "E16.1.2.3", {"start": v(-31.33, 185.62) * mm, "end": v(-31.33, 179.75) * mm});
            skLineSegment(sketch, "E16.1.3.0", {"start": v(-31.35, 189.53) * mm, "end": v(-26.48, 189.53) * mm});
            skLineSegment(sketch, "E16.1.3.1", {"start": v(-26.48, 195.4) * mm, "end": v(-26.48, 189.53) * mm});
            skArc(sketch, "E16.1.3.2", {"start": v(-26.48, 195.4) * mm, "mid": v(-28.91, 197.83) * mm, "end": v(-31.35, 195.4) * mm});
            skLineSegment(sketch, "E16.1.3.3", {"start": v(-31.35, 195.4) * mm, "end": v(-31.35, 189.53) * mm});
            skLineSegment(sketch, "E16.2.0.0", {"start": v(-20.82, 160.28) * mm, "end": v(-15.95, 160.28) * mm});
            skLineSegment(sketch, "E16.2.0.1", {"start": v(-15.95, 166.15) * mm, "end": v(-15.95, 160.28) * mm});
            skArc(sketch, "E16.2.0.2", {"start": v(-15.95, 166.15) * mm, "mid": v(-18.38, 168.58) * mm, "end": v(-20.82, 166.15) * mm});
            skLineSegment(sketch, "E16.2.0.3", {"start": v(-20.82, 166.15) * mm, "end": v(-20.82, 160.28) * mm});
            skLineSegment(sketch, "E16.2.1.0", {"start": v(-20.83, 170.05) * mm, "end": v(-15.96, 170.05) * mm});
            skLineSegment(sketch, "E16.2.1.1", {"start": v(-15.96, 175.92) * mm, "end": v(-15.96, 170.05) * mm});
            skArc(sketch, "E16.2.1.2", {"start": v(-15.96, 175.92) * mm, "mid": v(-18.4, 178.36) * mm, "end": v(-20.83, 175.92) * mm});
            skLineSegment(sketch, "E16.2.1.3", {"start": v(-20.83, 175.92) * mm, "end": v(-20.83, 170.05) * mm});
            skLineSegment(sketch, "E16.2.2.0", {"start": v(-20.85, 179.83) * mm, "end": v(-15.98, 179.83) * mm});
            skLineSegment(sketch, "E16.2.2.1", {"start": v(-15.98, 185.7) * mm, "end": v(-15.98, 179.83) * mm});
            skArc(sketch, "E16.2.2.2", {"start": v(-15.98, 185.7) * mm, "mid": v(-18.41, 188.13) * mm, "end": v(-20.85, 185.7) * mm});
            skLineSegment(sketch, "E16.2.2.3", {"start": v(-20.85, 185.7) * mm, "end": v(-20.85, 179.83) * mm});
            skLineSegment(sketch, "E16.2.3.0", {"start": v(-20.86, 189.6) * mm, "end": v(-16, 189.6) * mm});
            skLineSegment(sketch, "E16.2.3.1", {"start": v(-16, 195.48) * mm, "end": v(-16, 189.6) * mm});
            skArc(sketch, "E16.2.3.2", {"start": v(-16, 195.48) * mm, "mid": v(-18.43, 197.9) * mm, "end": v(-20.86, 195.48) * mm});
            skLineSegment(sketch, "E16.2.3.3", {"start": v(-20.86, 195.48) * mm, "end": v(-20.86, 189.6) * mm});
            skLineSegment(sketch, "E16.direction1", {"start": v(-41.78, 160.12) * mm, "end": v(-31.3, 160.2) * mm, "construction": true});
            skLineSegment(sketch, "E16.direction2", {"start": v(-41.78, 160.12) * mm, "end": v(-41.8, 169.9) * mm, "construction": true});
            skSolve(sketch);
        }
        {
            var Q0;
            Q0 = qSketchRegion(id + "F16", true);
            extrude(context, id + "F17", {"entities" : qUnion([Q0]), "operationType" : NewBodyOperationType.REMOVE, "endBound" : BoundingType.THROUGH_ALL, "oppositeDirection" : true, "depth" : 25 * mm});
        }
        {
            var Q0;
            Q0=makeQuery(id+"F5.opExtrude","SWEPT_FACE",FACE,{"disambiguationData":[OSD([sQuery(id+"F4.wireOp",EDGE,"E2.left")])]});
            var sketch = newSketch(context, id + "F18", { "sketchPlane" : qUnion([Q0])});
            skLineSegment(sketch, "E17.top", {"start": v(-27.96, 162.71) * mm, "end": v(-23.1, 162.71) * mm});
            skLineSegment(sketch, "E17.left", {"start": v(-27.96, 168.58) * mm, "end": v(-27.96, 162.71) * mm});
            skLineSegment(sketch, "E17.right", {"start": v(-23.1, 168.58) * mm, "end": v(-23.1, 162.71) * mm});
            skArc(sketch, "E18", {"start": v(-23.1, 168.58) * mm, "mid": v(-25.53, 171.02) * mm, "end": v(-27.96, 168.58) * mm});
            skLineSegment(sketch, "E19.0.1.0", {"start": v(-27.98, 172.49) * mm, "end": v(-23.1, 172.49) * mm});
            skLineSegment(sketch, "E19.0.1.1", {"start": v(-23.1, 178.36) * mm, "end": v(-23.1, 172.49) * mm});
            skArc(sketch, "E19.0.1.2", {"start": v(-23.1, 178.36) * mm, "mid": v(-25.54, 180.8) * mm, "end": v(-27.98, 178.36) * mm});
            skLineSegment(sketch, "E19.0.1.3", {"start": v(-27.98, 178.36) * mm, "end": v(-27.98, 172.49) * mm});
            skLineSegment(sketch, "E19.0.2.0", {"start": v(-28, 182.26) * mm, "end": v(-23.12, 182.26) * mm});
            skLineSegment(sketch, "E19.0.2.1", {"start": v(-23.12, 188.13) * mm, "end": v(-23.12, 182.26) * mm});
            skArc(sketch, "E19.0.2.2", {"start": v(-23.12, 188.13) * mm, "mid": v(-25.56, 190.57) * mm, "end": v(-28, 188.13) * mm});
            skLineSegment(sketch, "E19.0.2.3", {"start": v(-28, 188.13) * mm, "end": v(-28, 182.26) * mm});
            skLineSegment(sketch, "E19.0.3.0", {"start": v(-28, 192.04) * mm, "end": v(-23.14, 192.04) * mm});
            skLineSegment(sketch, "E19.0.3.1", {"start": v(-23.14, 197.9) * mm, "end": v(-23.14, 192.04) * mm});
            skArc(sketch, "E19.0.3.2", {"start": v(-23.14, 197.9) * mm, "mid": v(-25.57, 200.34) * mm, "end": v(-28, 197.9) * mm});
            skLineSegment(sketch, "E19.0.3.3", {"start": v(-28, 197.9) * mm, "end": v(-28, 192.04) * mm});
            skLineSegment(sketch, "E19.1.0.0", {"start": v(-17.48, 162.79) * mm, "end": v(-12.6, 162.79) * mm});
            skLineSegment(sketch, "E19.1.0.1", {"start": v(-12.6, 168.66) * mm, "end": v(-12.6, 162.79) * mm});
            skArc(sketch, "E19.1.0.2", {"start": v(-12.6, 168.66) * mm, "mid": v(-15.04, 171.1) * mm, "end": v(-17.48, 168.66) * mm});
            skLineSegment(sketch, "E19.1.0.3", {"start": v(-17.48, 168.66) * mm, "end": v(-17.48, 162.79) * mm});
            skLineSegment(sketch, "E19.1.1.0", {"start": v(-17.5, 172.56) * mm, "end": v(-12.62, 172.56) * mm});
            skLineSegment(sketch, "E19.1.1.1", {"start": v(-12.62, 178.43) * mm, "end": v(-12.62, 172.56) * mm});
            skArc(sketch, "E19.1.1.2", {"start": v(-12.62, 178.43) * mm, "mid": v(-15.06, 180.87) * mm, "end": v(-17.5, 178.43) * mm});
            skLineSegment(sketch, "E19.1.1.3", {"start": v(-17.5, 178.43) * mm, "end": v(-17.5, 172.56) * mm});
            skLineSegment(sketch, "E19.1.2.0", {"start": v(-17.5, 182.34) * mm, "end": v(-12.64, 182.34) * mm});
            skLineSegment(sketch, "E19.1.2.1", {"start": v(-12.64, 188.2) * mm, "end": v(-12.64, 182.34) * mm});
            skArc(sketch, "E19.1.2.2", {"start": v(-12.64, 188.2) * mm, "mid": v(-15.07, 190.64) * mm, "end": v(-17.5, 188.2) * mm});
            skLineSegment(sketch, "E19.1.2.3", {"start": v(-17.5, 188.2) * mm, "end": v(-17.5, 182.34) * mm});
            skLineSegment(sketch, "E19.1.3.0", {"start": v(-17.52, 192.12) * mm, "end": v(-12.65, 192.12) * mm});
            skLineSegment(sketch, "E19.1.3.1", {"start": v(-12.65, 197.99) * mm, "end": v(-12.65, 192.12) * mm});
            skArc(sketch, "E19.1.3.2", {"start": v(-12.65, 197.99) * mm, "mid": v(-15.09, 200.42) * mm, "end": v(-17.52, 197.99) * mm});
            skLineSegment(sketch, "E19.1.3.3", {"start": v(-17.52, 197.99) * mm, "end": v(-17.52, 192.12) * mm});
            skLineSegment(sketch, "E19.2.0.0", {"start": v(-7, 162.86) * mm, "end": v(-2.12, 162.86) * mm});
            skLineSegment(sketch, "E19.2.0.1", {"start": v(-2.12, 168.73) * mm, "end": v(-2.12, 162.86) * mm});
            skArc(sketch, "E19.2.0.2", {"start": v(-2.12, 168.73) * mm, "mid": v(-4.56, 171.17) * mm, "end": v(-7, 168.73) * mm});
            skLineSegment(sketch, "E19.2.0.3", {"start": v(-7, 168.73) * mm, "end": v(-7, 162.86) * mm});
            skLineSegment(sketch, "E19.2.1.0", {"start": v(-7, 172.64) * mm, "end": v(-2.14, 172.64) * mm});
            skLineSegment(sketch, "E19.2.1.1", {"start": v(-2.14, 178.5) * mm, "end": v(-2.14, 172.64) * mm});
            skArc(sketch, "E19.2.1.2", {"start": v(-2.14, 178.5) * mm, "mid": v(-4.57, 180.94) * mm, "end": v(-7, 178.5) * mm});
            skLineSegment(sketch, "E19.2.1.3", {"start": v(-7, 178.5) * mm, "end": v(-7, 172.64) * mm});
            skLineSegment(sketch, "E19.2.2.0", {"start": v(-7.02, 182.42) * mm, "end": v(-2.15, 182.42) * mm});
            skLineSegment(sketch, "E19.2.2.1", {"start": v(-2.15, 188.29) * mm, "end": v(-2.15, 182.42) * mm});
            skArc(sketch, "E19.2.2.2", {"start": v(-2.15, 188.29) * mm, "mid": v(-4.59, 190.72) * mm, "end": v(-7.02, 188.29) * mm});
            skLineSegment(sketch, "E19.2.2.3", {"start": v(-7.02, 188.29) * mm, "end": v(-7.02, 182.42) * mm});
            skLineSegment(sketch, "E19.2.3.0", {"start": v(-7.04, 192.2) * mm, "end": v(-2.17, 192.2) * mm});
            skLineSegment(sketch, "E19.2.3.1", {"start": v(-2.17, 198.06) * mm, "end": v(-2.17, 192.2) * mm});
            skArc(sketch, "E19.2.3.2", {"start": v(-2.17, 198.06) * mm, "mid": v(-4.6, 200.5) * mm, "end": v(-7.04, 198.06) * mm});
            skLineSegment(sketch, "E19.2.3.3", {"start": v(-7.04, 198.06) * mm, "end": v(-7.04, 192.2) * mm});
            skLineSegment(sketch, "E19.direction1", {"start": v(-27.96, 162.71) * mm, "end": v(-17.48, 162.79) * mm, "construction": true});
            skLineSegment(sketch, "E19.direction2", {"start": v(-27.96, 162.71) * mm, "end": v(-27.98, 172.49) * mm, "construction": true});
            skSolve(sketch);
        }
        {
            var Q0;
            Q0 = qSketchRegion(id + "F18", true);
            extrude(context, id + "F19", {"entities" : qUnion([Q0]), "operationType" : NewBodyOperationType.REMOVE, "endBound" : BoundingType.THROUGH_ALL, "oppositeDirection" : true, "depth" : 25 * mm});
        }
        {
            var Q0;
            Q0=makeQuery(id+"F1.opExtrude","CAP_FACE",FACE,{"disambiguationData":[OSD([sQuery(id+"F0.wireOp",EDGE,"E0.bottom"),sQuery(id+"F0.wireOp",EDGE,"E0.top"),sQuery(id+"F0.wireOp",EDGE,"E0.left"),sQuery(id+"F0.wireOp",EDGE,"E0.right")])],"isStart":false});
            var sketch = newSketch(context, id + "F20", { "sketchPlane" : qUnion([Q0])});
            skCircle(sketch, "E20", {"center": v(8.18, -30.66) * mm, "radius": 1.97 * mm});
            skSolve(sketch);
        }
        {
            var Q0;
            Q0=makeQuery(id+"F20.imprint","IMPRINT",FACE,{"disambiguationData":[TD([[makeQuery(id+"F20.imprint","IMPRINT",EDGE,{"derivedFrom":sQuery(id+"F20.wireOp",EDGE,"E20")}),1.0]])]});
            extrude(context, id + "F21", {"entities" : qUnion([Q0]), "operationType" : NewBodyOperationType.ADD, "depth" : 5 * mm});
        }
        {
            var Q0;
            Q0=makeQuery(id+"F21.opExtrude","CAP_FACE",FACE,{"disambiguationData":[OSD([sQuery(id+"F20.wireOp",EDGE,"E20")])],"isStart":false});
            var sketch = newSketch(context, id + "F22", { "sketchPlane" : qUnion([Q0])});
            skCircle(sketch, "E21", {"center": v(8.18, -30.66) * mm, "radius": 10.55 * mm});
            skSolve(sketch);
        }
        {
            var Q0;
            Q0 = qSketchRegion(id + "F22", true);
            extrude(context, id + "F23", {"entities" : qUnion([Q0]), "operationType" : NewBodyOperationType.ADD, "depth" : 25 * mm, "hasDraft" : true, "draftAngle" : 22 * degree, "draftPullDirection" : true});
        }
    });
